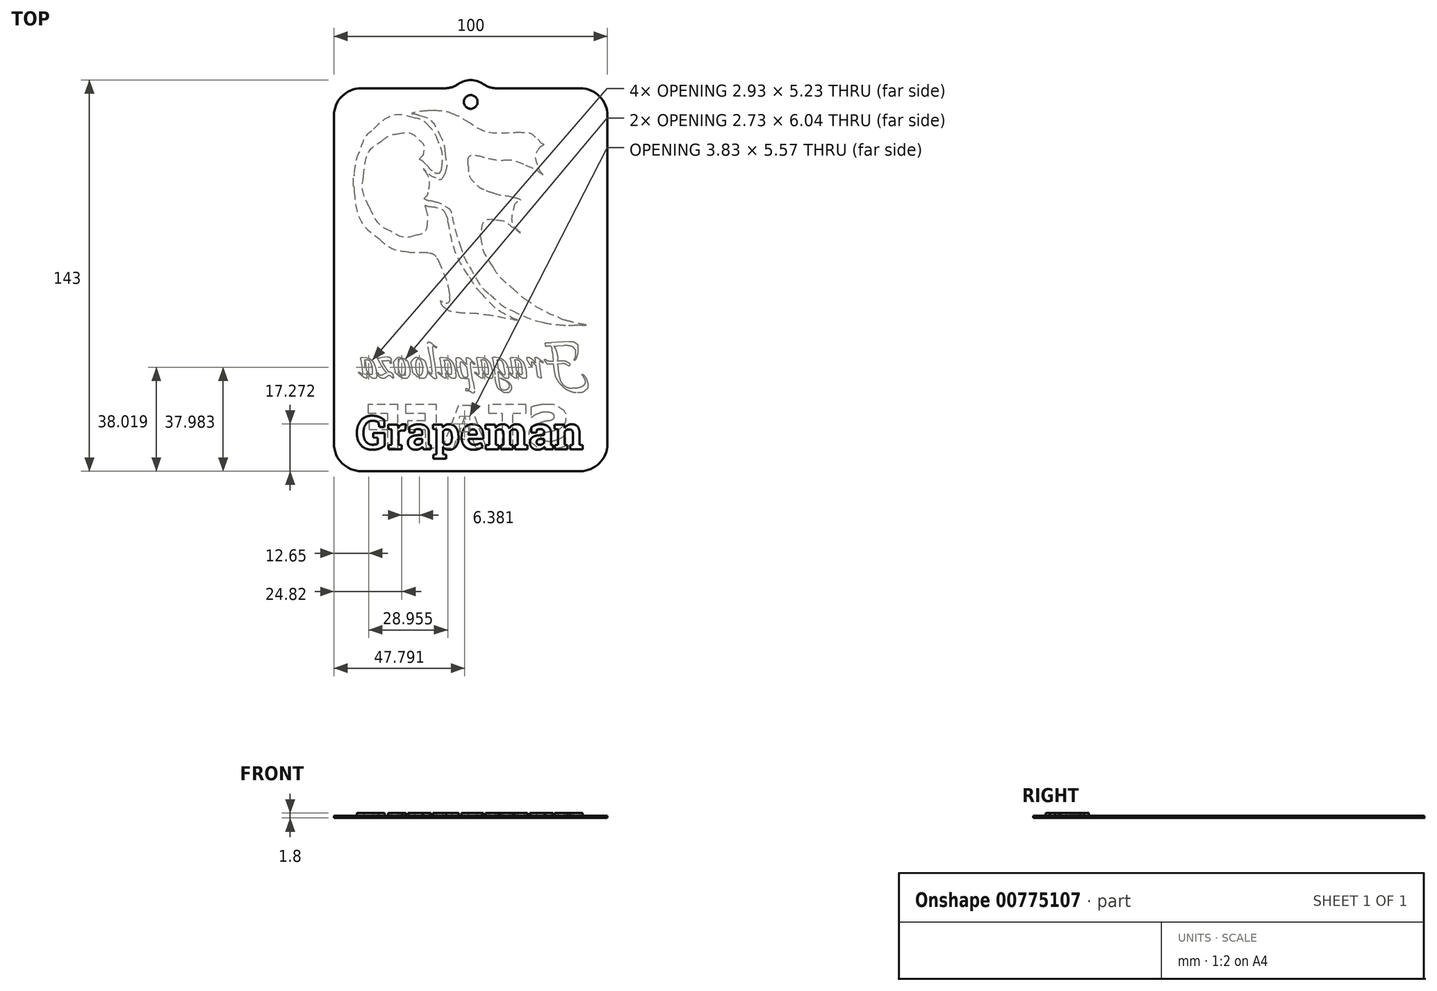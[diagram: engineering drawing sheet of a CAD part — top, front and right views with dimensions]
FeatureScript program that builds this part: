
annotation { "Feature Type Name" : "Feature", "Feature Type Description" : "" }
export const myFeature = defineFeature(function(context is Context, id is Id, definition is map)
    precondition{}
    {
        {
            var Q0;
            Q0=qCreatedBy(makeId("Top.planeOp"),FACE);
            var sketch = newSketch(context, id + "F0", { "sketchPlane" : qUnion([Q0])});
            skLineSegment(sketch, "E0.bottom", {"start": v(-40, 70) * mm, "end": v(-9.33, 70) * mm});
            skLineSegment(sketch, "E0.top", {"start": v(-40, -70) * mm, "end": v(40, -70) * mm});
            skLineSegment(sketch, "E0.left", {"start": v(-50, 60) * mm, "end": v(-50, -60) * mm});
            skLineSegment(sketch, "E0.right", {"start": v(50, 60) * mm, "end": v(50, -60) * mm});
            skPoint(sketch, "E0.middle", {"position": v(0, 0) * mm});
            skCircle(sketch, "E1", {"center": v(0, 65) * mm, "radius": 2.5 * mm});
            skPoint(sketch, "E2.visualSharp", {"position": v(-50, 70) * mm});
            skArc(sketch, "E2.filletArc", {"start": v(-40, 70) * mm, "mid": v(-47.07, 67.07) * mm, "end": v(-50, 60) * mm});
            skPoint(sketch, "E3.visualSharp", {"position": v(50, 70) * mm});
            skArc(sketch, "E3.filletArc", {"start": v(50, 60) * mm, "mid": v(47.07, 67.07) * mm, "end": v(40, 70) * mm});
            skPoint(sketch, "E4.visualSharp", {"position": v(50, -70) * mm});
            skArc(sketch, "E4.filletArc", {"start": v(40, -70) * mm, "mid": v(47.07, -67.07) * mm, "end": v(50, -60) * mm});
            skPoint(sketch, "E5.visualSharp", {"position": v(-50, -70) * mm});
            skArc(sketch, "E5.filletArc", {"start": v(-50, -60) * mm, "mid": v(-47.07, -67.07) * mm, "end": v(-40, -70) * mm});
            skArc(sketch, "E6", {"start": v(-4.66, 71.5) * mm, "mid": v(0, 73) * mm, "end": v(4.66, 71.5) * mm});
            skArc(sketch, "E7.filletArc", {"start": v(-9.33, 70) * mm, "mid": v(-6.88, 70.38) * mm, "end": v(-4.66, 71.5) * mm});
            skLineSegment(sketch, "E8", {"start": v(40, 70) * mm, "end": v(9.33, 70) * mm});
            skArc(sketch, "E9.filletArc", {"start": v(4.66, 71.5) * mm, "mid": v(6.88, 70.38) * mm, "end": v(9.33, 70) * mm});
            skSolve(sketch);
        }
        {
            var Q0;
            Q0=qCreatedBy(makeId("Top.planeOp"),FACE);
            var sketch = newSketch(context, id + "F1", { "sketchPlane" : qUnion([Q0])});
            skLineSegment(sketch, "E10", {"start": v(38.17, -16.7) * mm, "end": v(38.78, -16.7) * mm});
            skLineSegment(sketch, "E11", {"start": v(-13.07, 61.96) * mm, "end": v(-13.17, 61.96) * mm});
            skLineSegment(sketch, "E12", {"start": v(-14.17, 61.96) * mm, "end": v(-14.37, 61.96) * mm});
            skLineSegment(sketch, "E13", {"start": v(-42.85, 37.93) * mm, "end": v(-42.85, 36.81) * mm});
            skLineSegment(sketch, "E14", {"start": v(-42.85, 35.49) * mm, "end": v(-42.85, 34.98) * mm});
            skLineSegment(sketch, "E15", {"start": v(-42.85, 34.78) * mm, "end": v(-42.85, 34.16) * mm});
            skLineSegment(sketch, "E16", {"start": v(40.64, -16.7) * mm, "end": v(40.63, -16.62) * mm});
            skLineSegment(sketch, "E17", {"start": v(38.83, -16.7) * mm, "end": v(40.64, -16.7) * mm});
            skLineSegment(sketch, "E18", {"start": v(-42.85, 36.81) * mm, "end": v(-42.85, 35.49) * mm});
            skLineSegment(sketch, "E19", {"start": v(-13.21, 61.96) * mm, "end": v(-14.22, 61.96) * mm});
            skLineSegment(sketch, "E20", {"start": v(-42.85, 34.98) * mm, "end": v(-42.85, 34.77) * mm});
            skLineSegment(sketch, "E21", {"start": v(36.03, -31.52) * mm, "end": v(35.01, -30.98) * mm});
            skLineSegment(sketch, "E22", {"start": v(33.37, -30.7) * mm, "end": v(32.17, -30.75) * mm});
            skLineSegment(sketch, "E23", {"start": v(32.17, -30.75) * mm, "end": v(30.92, -30.82) * mm});
            skLineSegment(sketch, "E24", {"start": v(30.92, -30.82) * mm, "end": v(27.9, -30.82) * mm});
            skLineSegment(sketch, "E25", {"start": v(27.9, -30.82) * mm, "end": v(27.52, -30.26) * mm});
            skLineSegment(sketch, "E26", {"start": v(26.88, -29.35) * mm, "end": v(26.9, -29.28) * mm});
            skLineSegment(sketch, "E27", {"start": v(30.32, -29.76) * mm, "end": v(31.57, -29.76) * mm});
            skLineSegment(sketch, "E28", {"start": v(31.57, -29.76) * mm, "end": v(33.15, -29.76) * mm});
            skLineSegment(sketch, "E29", {"start": v(33.15, -29.76) * mm, "end": v(34.41, -29.76) * mm});
            skLineSegment(sketch, "E30", {"start": v(34.05, -24.06) * mm, "end": v(31.6, -24.16) * mm});
            skLineSegment(sketch, "E31", {"start": v(31.6, -24.16) * mm, "end": v(29.36, -24.3) * mm});
            skLineSegment(sketch, "E32", {"start": v(27.3, -24.39) * mm, "end": v(27.09, -23.13) * mm});
            skLineSegment(sketch, "E33", {"start": v(29.45, -22.97) * mm, "end": v(31.35, -22.93) * mm});
            skLineSegment(sketch, "E34", {"start": v(31.35, -22.93) * mm, "end": v(33.78, -22.78) * mm});
            skLineSegment(sketch, "E35", {"start": v(33.78, -22.78) * mm, "end": v(36.14, -22.66) * mm});
            skLineSegment(sketch, "E36", {"start": v(38.04, -29.5) * mm, "end": v(37.7, -29.32) * mm});
            skLineSegment(sketch, "E37", {"start": v(30.25, -30.2) * mm, "end": v(29.88, -26.54) * mm});
            skLineSegment(sketch, "E38", {"start": v(29.55, -24.56) * mm, "end": v(29.3, -24.3) * mm});
            skLineSegment(sketch, "E39", {"start": v(29.18, -23.96) * mm, "end": v(29.55, -24.04) * mm});
            skLineSegment(sketch, "E40", {"start": v(31.76, -29.06) * mm, "end": v(31.88, -31.82) * mm});
            skLineSegment(sketch, "E41", {"start": v(37.27, -39.71) * mm, "end": v(38.3, -39.63) * mm});
            skLineSegment(sketch, "E42", {"start": v(41.15, -35.4) * mm, "end": v(40.78, -34.92) * mm});
            skLineSegment(sketch, "E43", {"start": v(40.78, -34.92) * mm, "end": v(40.72, -34.76) * mm});
            skLineSegment(sketch, "E44", {"start": v(23.56, -29.53) * mm, "end": v(23.5, -28.89) * mm});
            skLineSegment(sketch, "E45", {"start": v(24.23, -28.54) * mm, "end": v(25.22, -29.23) * mm});
            skLineSegment(sketch, "E46", {"start": v(25.22, -29.23) * mm, "end": v(26.33, -30.01) * mm});
            skLineSegment(sketch, "E47", {"start": v(26.48, -30.3) * mm, "end": v(26.4, -30.34) * mm});
            skLineSegment(sketch, "E48", {"start": v(26.4, -30.34) * mm, "end": v(26.3, -30.32) * mm});
            skLineSegment(sketch, "E49", {"start": v(26.3, -30.32) * mm, "end": v(26.17, -30.3) * mm});
            skLineSegment(sketch, "E50", {"start": v(25.15, -30.3) * mm, "end": v(25.53, -33.54) * mm});
            skLineSegment(sketch, "E51", {"start": v(25.53, -33.54) * mm, "end": v(25.79, -35.64) * mm});
            skLineSegment(sketch, "E52", {"start": v(25.88, -36) * mm, "end": v(24.4, -35.44) * mm});
            skLineSegment(sketch, "E53", {"start": v(23.19, -29.85) * mm, "end": v(23.89, -30.75) * mm});
            skLineSegment(sketch, "E54", {"start": v(23.65, -31.18) * mm, "end": v(23.19, -30.77) * mm});
            skLineSegment(sketch, "E55", {"start": v(15.9, -29.4) * mm, "end": v(15.4, -29.4) * mm});
            skLineSegment(sketch, "E56", {"start": v(15.4, -29.4) * mm, "end": v(15.02, -29.33) * mm});
            skLineSegment(sketch, "E57", {"start": v(15.24, -28.42) * mm, "end": v(16.71, -28.55) * mm});
            skLineSegment(sketch, "E58", {"start": v(17.3, -34.56) * mm, "end": v(16.63, -33.84) * mm});
            skLineSegment(sketch, "E59", {"start": v(16.01, -32.3) * mm, "end": v(16.46, -32.84) * mm});
            skLineSegment(sketch, "E60", {"start": v(16.96, -29.4) * mm, "end": v(16.5, -29.4) * mm});
            skLineSegment(sketch, "E61", {"start": v(16.5, -29.4) * mm, "end": v(15.9, -29.4) * mm});
            skLineSegment(sketch, "E62", {"start": v(16.38, -31.1) * mm, "end": v(16.6, -32.79) * mm});
            skLineSegment(sketch, "E63", {"start": v(16.6, -32.79) * mm, "end": v(16.8, -34.4) * mm});
            skLineSegment(sketch, "E64", {"start": v(16.8, -34.4) * mm, "end": v(16.85, -35.3) * mm});
            skLineSegment(sketch, "E65", {"start": v(14.85, -34.45) * mm, "end": v(15.26, -34.75) * mm});
            skLineSegment(sketch, "E66", {"start": v(15.33, -34.51) * mm, "end": v(15.26, -33.72) * mm});
            skLineSegment(sketch, "E67", {"start": v(15.26, -33.72) * mm, "end": v(14.93, -31.64) * mm});
            skLineSegment(sketch, "E68", {"start": v(14.93, -31.64) * mm, "end": v(14.54, -29.14) * mm});
            skLineSegment(sketch, "E69", {"start": v(9.13, -29.4) * mm, "end": v(8.63, -29.4) * mm});
            skLineSegment(sketch, "E70", {"start": v(8.63, -29.4) * mm, "end": v(8.27, -29.31) * mm});
            skLineSegment(sketch, "E71", {"start": v(8.04, -29.08) * mm, "end": v(7.89, -28.74) * mm});
            skLineSegment(sketch, "E72", {"start": v(8.47, -28.35) * mm, "end": v(8.95, -28.35) * mm});
            skLineSegment(sketch, "E73", {"start": v(8.95, -28.35) * mm, "end": v(9.46, -28.52) * mm});
            skLineSegment(sketch, "E74", {"start": v(9.46, -28.52) * mm, "end": v(10.14, -28.6) * mm});
            skLineSegment(sketch, "E75", {"start": v(11.28, -34.74) * mm, "end": v(10.47, -33.88) * mm});
            skLineSegment(sketch, "E76", {"start": v(9.69, -32.05) * mm, "end": v(10.37, -32.95) * mm});
            skLineSegment(sketch, "E77", {"start": v(10.37, -32.95) * mm, "end": v(11.14, -33.94) * mm});
            skLineSegment(sketch, "E78", {"start": v(12.6, -34.13) * mm, "end": v(12.52, -33.32) * mm});
            skLineSegment(sketch, "E79", {"start": v(12.52, -33.32) * mm, "end": v(12.29, -32.26) * mm});
            skLineSegment(sketch, "E80", {"start": v(12.29, -32.26) * mm, "end": v(12.13, -31.6) * mm});
            skLineSegment(sketch, "E81", {"start": v(10.33, -29.4) * mm, "end": v(9.77, -29.4) * mm});
            skLineSegment(sketch, "E82", {"start": v(9.77, -29.4) * mm, "end": v(9.13, -29.4) * mm});
            skLineSegment(sketch, "E83", {"start": v(9.46, -28.84) * mm, "end": v(9.77, -30.97) * mm});
            skLineSegment(sketch, "E84", {"start": v(9.77, -30.97) * mm, "end": v(10.1, -34.04) * mm});
            skLineSegment(sketch, "E85", {"start": v(10.1, -34.04) * mm, "end": v(10.34, -36.29) * mm});
            skLineSegment(sketch, "E86", {"start": v(10.34, -36.29) * mm, "end": v(10.47, -37.68) * mm});
            skLineSegment(sketch, "E87", {"start": v(12.25, -36.7) * mm, "end": v(11.22, -36.28) * mm});
            skLineSegment(sketch, "E88", {"start": v(10.66, -36) * mm, "end": v(10.7, -35.94) * mm});
            skLineSegment(sketch, "E89", {"start": v(8.88, -35.3) * mm, "end": v(8.5, -31.75) * mm});
            skLineSegment(sketch, "E90", {"start": v(3.54, -29.4) * mm, "end": v(3.04, -29.4) * mm});
            skLineSegment(sketch, "E91", {"start": v(3.04, -29.4) * mm, "end": v(2.67, -29.33) * mm});
            skLineSegment(sketch, "E92", {"start": v(2.88, -28.42) * mm, "end": v(4.36, -28.55) * mm});
            skLineSegment(sketch, "E93", {"start": v(4.94, -34.56) * mm, "end": v(4.28, -33.84) * mm});
            skLineSegment(sketch, "E94", {"start": v(3.66, -32.3) * mm, "end": v(4.1, -32.84) * mm});
            skLineSegment(sketch, "E95", {"start": v(4.6, -29.4) * mm, "end": v(4.14, -29.4) * mm});
            skLineSegment(sketch, "E96", {"start": v(4.14, -29.4) * mm, "end": v(3.54, -29.4) * mm});
            skLineSegment(sketch, "E97", {"start": v(4.02, -31.1) * mm, "end": v(4.25, -32.79) * mm});
            skLineSegment(sketch, "E98", {"start": v(4.25, -32.79) * mm, "end": v(4.44, -34.4) * mm});
            skLineSegment(sketch, "E99", {"start": v(4.44, -34.4) * mm, "end": v(4.5, -35.3) * mm});
            skLineSegment(sketch, "E100", {"start": v(2.5, -34.45) * mm, "end": v(2.9, -34.75) * mm});
            skLineSegment(sketch, "E101", {"start": v(2.98, -34.51) * mm, "end": v(2.9, -33.72) * mm});
            skLineSegment(sketch, "E102", {"start": v(2.9, -33.72) * mm, "end": v(2.58, -31.64) * mm});
            skLineSegment(sketch, "E103", {"start": v(2.58, -31.64) * mm, "end": v(2.19, -29.14) * mm});
            skLineSegment(sketch, "E104", {"start": v(-0.07, -30.77) * mm, "end": v(0.03, -32.01) * mm});
            skLineSegment(sketch, "E105", {"start": v(0.03, -32.01) * mm, "end": v(0.35, -34.14) * mm});
            skLineSegment(sketch, "E106", {"start": v(0.35, -34.14) * mm, "end": v(0.85, -37.11) * mm});
            skLineSegment(sketch, "E107", {"start": v(0.96, -41.4) * mm, "end": v(0.32, -41.16) * mm});
            skLineSegment(sketch, "E108", {"start": v(-0.43, -39.67) * mm, "end": v(-0.47, -38.83) * mm});
            skLineSegment(sketch, "E109", {"start": v(-0.47, -38.83) * mm, "end": v(-0.77, -36.7) * mm});
            skLineSegment(sketch, "E110", {"start": v(-0.77, -36.7) * mm, "end": v(-1.14, -33.74) * mm});
            skLineSegment(sketch, "E111", {"start": v(-1.14, -33.74) * mm, "end": v(-1.34, -32.16) * mm});
            skLineSegment(sketch, "E112", {"start": v(-1.34, -32.16) * mm, "end": v(-1.56, -30.34) * mm});
            skLineSegment(sketch, "E113", {"start": v(-1.56, -30.34) * mm, "end": v(-1.62, -29.37) * mm});
            skLineSegment(sketch, "E114", {"start": v(-0.41, -35.45) * mm, "end": v(-0.36, -35.65) * mm});
            skLineSegment(sketch, "E115", {"start": v(-0.18, -36.1) * mm, "end": v(-0.24, -36.16) * mm});
            skLineSegment(sketch, "E116", {"start": v(-0.24, -36.16) * mm, "end": v(-0.31, -36.19) * mm});
            skLineSegment(sketch, "E117", {"start": v(-0.31, -36.19) * mm, "end": v(-0.7, -36.11) * mm});
            skLineSegment(sketch, "E118", {"start": v(-0.7, -36.11) * mm, "end": v(-1.4, -36.11) * mm});
            skLineSegment(sketch, "E119", {"start": v(-1.4, -36.11) * mm, "end": v(-2.27, -36.11) * mm});
            skLineSegment(sketch, "E120", {"start": v(-2.53, -30.03) * mm, "end": v(-1.85, -30.67) * mm});
            skLineSegment(sketch, "E121", {"start": v(-9.94, -29.4) * mm, "end": v(-10.44, -29.4) * mm});
            skLineSegment(sketch, "E122", {"start": v(-10.44, -29.4) * mm, "end": v(-10.8, -29.33) * mm});
            skLineSegment(sketch, "E123", {"start": v(-10.6, -28.42) * mm, "end": v(-9.12, -28.55) * mm});
            skLineSegment(sketch, "E124", {"start": v(-8.54, -34.56) * mm, "end": v(-9.2, -33.84) * mm});
            skLineSegment(sketch, "E125", {"start": v(-9.82, -32.3) * mm, "end": v(-9.37, -32.84) * mm});
            skLineSegment(sketch, "E126", {"start": v(-8.87, -29.4) * mm, "end": v(-9.34, -29.4) * mm});
            skLineSegment(sketch, "E127", {"start": v(-9.34, -29.4) * mm, "end": v(-9.94, -29.4) * mm});
            skLineSegment(sketch, "E128", {"start": v(-9.46, -31.1) * mm, "end": v(-9.23, -32.79) * mm});
            skLineSegment(sketch, "E129", {"start": v(-9.23, -32.79) * mm, "end": v(-9.04, -34.4) * mm});
            skLineSegment(sketch, "E130", {"start": v(-9.04, -34.4) * mm, "end": v(-8.99, -35.3) * mm});
            skLineSegment(sketch, "E131", {"start": v(-10.98, -34.45) * mm, "end": v(-10.58, -34.75) * mm});
            skLineSegment(sketch, "E132", {"start": v(-10.5, -34.51) * mm, "end": v(-10.58, -33.72) * mm});
            skLineSegment(sketch, "E133", {"start": v(-10.58, -33.72) * mm, "end": v(-10.9, -31.64) * mm});
            skLineSegment(sketch, "E134", {"start": v(-10.9, -31.64) * mm, "end": v(-11.29, -29.14) * mm});
            skLineSegment(sketch, "E135", {"start": v(-14.16, -33.74) * mm, "end": v(-14.26, -32.52) * mm});
            skLineSegment(sketch, "E136", {"start": v(-14.26, -32.52) * mm, "end": v(-14.56, -30.46) * mm});
            skLineSegment(sketch, "E137", {"start": v(-14.56, -30.46) * mm, "end": v(-15.08, -27.43) * mm});
            skLineSegment(sketch, "E138", {"start": v(-15, -22.92) * mm, "end": v(-14.03, -23.56) * mm});
            skLineSegment(sketch, "E139", {"start": v(-12.63, -24.87) * mm, "end": v(-12.86, -24.8) * mm});
            skLineSegment(sketch, "E140", {"start": v(-13.91, -24.76) * mm, "end": v(-13.85, -25.5) * mm});
            skLineSegment(sketch, "E141", {"start": v(-13.85, -25.5) * mm, "end": v(-13.65, -26.9) * mm});
            skLineSegment(sketch, "E142", {"start": v(-13.65, -26.9) * mm, "end": v(-13.36, -28.73) * mm});
            skLineSegment(sketch, "E143", {"start": v(-13.36, -28.73) * mm, "end": v(-13.08, -30.79) * mm});
            skLineSegment(sketch, "E144", {"start": v(-13.08, -30.79) * mm, "end": v(-12.8, -32.84) * mm});
            skLineSegment(sketch, "E145", {"start": v(-12.8, -32.84) * mm, "end": v(-12.61, -34.45) * mm});
            skLineSegment(sketch, "E146", {"start": v(-12.61, -34.45) * mm, "end": v(-12.55, -35.39) * mm});
            skLineSegment(sketch, "E147", {"start": v(-19.13, -35.54) * mm, "end": v(-20.12, -34.9) * mm});
            skLineSegment(sketch, "E148", {"start": v(-21.26, -33.55) * mm, "end": v(-21.5, -32.5) * mm});
            skLineSegment(sketch, "E149", {"start": v(-21.5, -32.5) * mm, "end": v(-21.73, -31.52) * mm});
            skLineSegment(sketch, "E150", {"start": v(-21.73, -31.52) * mm, "end": v(-21.79, -30.84) * mm});
            skLineSegment(sketch, "E151", {"start": v(-19.8, -28.37) * mm, "end": v(-19.36, -28.42) * mm});
            skLineSegment(sketch, "E152", {"start": v(-19.36, -28.42) * mm, "end": v(-18.37, -28.75) * mm});
            skLineSegment(sketch, "E153", {"start": v(-17.54, -31.66) * mm, "end": v(-18, -30.05) * mm});
            skLineSegment(sketch, "E154", {"start": v(-25.5, -35.54) * mm, "end": v(-26.5, -34.9) * mm});
            skLineSegment(sketch, "E155", {"start": v(-27.64, -33.55) * mm, "end": v(-27.88, -32.5) * mm});
            skLineSegment(sketch, "E156", {"start": v(-27.88, -32.5) * mm, "end": v(-28.1, -31.52) * mm});
            skLineSegment(sketch, "E157", {"start": v(-28.1, -31.52) * mm, "end": v(-28.17, -30.84) * mm});
            skLineSegment(sketch, "E158", {"start": v(-26.19, -28.37) * mm, "end": v(-25.74, -28.42) * mm});
            skLineSegment(sketch, "E159", {"start": v(-25.74, -28.42) * mm, "end": v(-24.75, -28.75) * mm});
            skLineSegment(sketch, "E160", {"start": v(-23.92, -31.66) * mm, "end": v(-24.38, -30.05) * mm});
            skLineSegment(sketch, "E161", {"start": v(-30.82, -29.63) * mm, "end": v(-31.6, -29.66) * mm});
            skLineSegment(sketch, "E162", {"start": v(-31.6, -29.66) * mm, "end": v(-32.28, -29.63) * mm});
            skLineSegment(sketch, "E163", {"start": v(-32.28, -29.63) * mm, "end": v(-32.6, -29.59) * mm});
            skLineSegment(sketch, "E164", {"start": v(-28.05, -35.7) * mm, "end": v(-28.34, -36) * mm});
            skLineSegment(sketch, "E165", {"start": v(-32.16, -32.19) * mm, "end": v(-32.67, -31.4) * mm});
            skLineSegment(sketch, "E166", {"start": v(-32.67, -31.4) * mm, "end": v(-33.23, -30.44) * mm});
            skLineSegment(sketch, "E167", {"start": v(-33.23, -30.44) * mm, "end": v(-33.8, -29.45) * mm});
            skLineSegment(sketch, "E168", {"start": v(-33.8, -29.45) * mm, "end": v(-34.28, -28.64) * mm});
            skLineSegment(sketch, "E169", {"start": v(-34.18, -28.33) * mm, "end": v(-34.02, -28.38) * mm});
            skLineSegment(sketch, "E170", {"start": v(-33.17, -28.56) * mm, "end": v(-32.43, -28.52) * mm});
            skLineSegment(sketch, "E171", {"start": v(-32.43, -28.52) * mm, "end": v(-31.52, -28.4) * mm});
            skLineSegment(sketch, "E172", {"start": v(-31.52, -28.4) * mm, "end": v(-30.4, -28.23) * mm});
            skLineSegment(sketch, "E173", {"start": v(-29.1, -29.33) * mm, "end": v(-29.02, -30) * mm});
            skLineSegment(sketch, "E174", {"start": v(-28.09, -35.68) * mm, "end": v(-28.22, -35.85) * mm});
            skLineSegment(sketch, "E175", {"start": v(-28.4, -35.95) * mm, "end": v(-29.27, -35.27) * mm});
            skLineSegment(sketch, "E176", {"start": v(-32.12, -34.67) * mm, "end": v(-31.13, -34.22) * mm});
            skLineSegment(sketch, "E177", {"start": v(-31.13, -34.22) * mm, "end": v(-30.22, -33.8) * mm});
            skLineSegment(sketch, "E178", {"start": v(-28.36, -35.08) * mm, "end": v(-28.32, -35.29) * mm});
            skLineSegment(sketch, "E179", {"start": v(-28.32, -35.29) * mm, "end": v(-28.26, -35.48) * mm});
            skLineSegment(sketch, "E180", {"start": v(-28.26, -35.48) * mm, "end": v(-28.09, -35.68) * mm});
            skLineSegment(sketch, "E181", {"start": v(-38.9, -29.4) * mm, "end": v(-39.4, -29.4) * mm});
            skLineSegment(sketch, "E182", {"start": v(-39.4, -29.4) * mm, "end": v(-39.76, -29.33) * mm});
            skLineSegment(sketch, "E183", {"start": v(-39.55, -28.42) * mm, "end": v(-38.08, -28.55) * mm});
            skLineSegment(sketch, "E184", {"start": v(-37.5, -34.56) * mm, "end": v(-38.15, -33.84) * mm});
            skLineSegment(sketch, "E185", {"start": v(-38.77, -32.3) * mm, "end": v(-38.33, -32.84) * mm});
            skLineSegment(sketch, "E186", {"start": v(-37.82, -29.4) * mm, "end": v(-38.3, -29.4) * mm});
            skLineSegment(sketch, "E187", {"start": v(-38.3, -29.4) * mm, "end": v(-38.9, -29.4) * mm});
            skLineSegment(sketch, "E188", {"start": v(-38.41, -31.1) * mm, "end": v(-38.19, -32.79) * mm});
            skLineSegment(sketch, "E189", {"start": v(-38.19, -32.79) * mm, "end": v(-38, -34.4) * mm});
            skLineSegment(sketch, "E190", {"start": v(-38, -34.4) * mm, "end": v(-37.94, -35.3) * mm});
            skLineSegment(sketch, "E191", {"start": v(-39.94, -34.45) * mm, "end": v(-39.53, -34.75) * mm});
            skLineSegment(sketch, "E192", {"start": v(-39.45, -34.51) * mm, "end": v(-39.53, -33.72) * mm});
            skLineSegment(sketch, "E193", {"start": v(-39.53, -33.72) * mm, "end": v(-39.86, -31.64) * mm});
            skLineSegment(sketch, "E194", {"start": v(-39.86, -31.64) * mm, "end": v(-40.24, -29.14) * mm});
            skLineSegment(sketch, "E195", {"start": v(22.49, -50.22) * mm, "end": v(22.06, -50.22) * mm});
            skLineSegment(sketch, "E196", {"start": v(22.06, -50.22) * mm, "end": v(22.06, -46.56) * mm});
            skLineSegment(sketch, "E197", {"start": v(34.32, -56.92) * mm, "end": v(34.76, -56.92) * mm});
            skLineSegment(sketch, "E198", {"start": v(34.76, -56.92) * mm, "end": v(34.76, -60.73) * mm});
            skLineSegment(sketch, "E199", {"start": v(6.54, -45.64) * mm, "end": v(20.3, -45.64) * mm});
            skLineSegment(sketch, "E200", {"start": v(20.3, -45.64) * mm, "end": v(20.3, -48.81) * mm});
            skLineSegment(sketch, "E201", {"start": v(20.3, -48.81) * mm, "end": v(15.36, -48.81) * mm});
            skLineSegment(sketch, "E202", {"start": v(15.36, -48.81) * mm, "end": v(15.36, -61.51) * mm});
            skLineSegment(sketch, "E203", {"start": v(15.36, -61.51) * mm, "end": v(11.47, -61.51) * mm});
            skLineSegment(sketch, "E204", {"start": v(11.47, -61.51) * mm, "end": v(11.47, -48.81) * mm});
            skLineSegment(sketch, "E205", {"start": v(11.47, -48.81) * mm, "end": v(6.54, -48.81) * mm});
            skLineSegment(sketch, "E206", {"start": v(6.54, -48.81) * mm, "end": v(6.54, -45.64) * mm});
            skLineSegment(sketch, "E207", {"start": v(-4.56, -45.99) * mm, "end": v(0.04, -45.99) * mm});
            skLineSegment(sketch, "E208", {"start": v(0.04, -45.99) * mm, "end": v(5.78, -61.51) * mm});
            skLineSegment(sketch, "E209", {"start": v(5.78, -61.51) * mm, "end": v(1.8, -61.51) * mm});
            skLineSegment(sketch, "E210", {"start": v(1.8, -61.51) * mm, "end": v(0.7, -58.34) * mm});
            skLineSegment(sketch, "E211", {"start": v(0.7, -58.34) * mm, "end": v(-5.12, -58.34) * mm});
            skLineSegment(sketch, "E212", {"start": v(-5.12, -58.34) * mm, "end": v(-6.2, -61.51) * mm});
            skLineSegment(sketch, "E213", {"start": v(-6.2, -61.51) * mm, "end": v(-10.3, -61.51) * mm});
            skLineSegment(sketch, "E214", {"start": v(-10.3, -61.51) * mm, "end": v(-4.56, -45.99) * mm});
            skLineSegment(sketch, "E215", {"start": v(-0.3, -55.51) * mm, "end": v(-2.2, -49.94) * mm});
            skLineSegment(sketch, "E216", {"start": v(-2.2, -49.94) * mm, "end": v(-4.12, -55.51) * mm});
            skLineSegment(sketch, "E217", {"start": v(-4.12, -55.51) * mm, "end": v(-0.3, -55.51) * mm});
            skLineSegment(sketch, "E218", {"start": v(-23.8, -45.64) * mm, "end": v(-12.51, -45.64) * mm});
            skLineSegment(sketch, "E219", {"start": v(-12.51, -45.64) * mm, "end": v(-12.51, -61.51) * mm});
            skLineSegment(sketch, "E220", {"start": v(-12.51, -61.51) * mm, "end": v(-16.4, -61.51) * mm});
            skLineSegment(sketch, "E221", {"start": v(-16.4, -61.51) * mm, "end": v(-16.75, -54.8) * mm});
            skLineSegment(sketch, "E222", {"start": v(-16.75, -54.8) * mm, "end": v(-23.1, -54.8) * mm});
            skLineSegment(sketch, "E223", {"start": v(-23.1, -54.8) * mm, "end": v(-23.1, -51.63) * mm});
            skLineSegment(sketch, "E224", {"start": v(-23.1, -51.63) * mm, "end": v(-16.75, -51.63) * mm});
            skLineSegment(sketch, "E225", {"start": v(-16.75, -51.63) * mm, "end": v(-16.75, -48.81) * mm});
            skLineSegment(sketch, "E226", {"start": v(-16.75, -48.81) * mm, "end": v(-23.8, -48.81) * mm});
            skLineSegment(sketch, "E227", {"start": v(-23.8, -48.81) * mm, "end": v(-23.8, -45.64) * mm});
            skLineSegment(sketch, "E228", {"start": v(-37.56, -45.64) * mm, "end": v(-26.63, -45.64) * mm});
            skLineSegment(sketch, "E229", {"start": v(-26.63, -45.64) * mm, "end": v(-26.63, -61.51) * mm});
            skLineSegment(sketch, "E230", {"start": v(-26.63, -61.51) * mm, "end": v(-30.5, -61.51) * mm});
            skLineSegment(sketch, "E231", {"start": v(-30.5, -61.51) * mm, "end": v(-30.5, -54.8) * mm});
            skLineSegment(sketch, "E232", {"start": v(-30.5, -54.8) * mm, "end": v(-37.2, -54.8) * mm});
            skLineSegment(sketch, "E233", {"start": v(-37.2, -54.8) * mm, "end": v(-37.2, -51.63) * mm});
            skLineSegment(sketch, "E234", {"start": v(-37.2, -51.63) * mm, "end": v(-30.5, -51.63) * mm});
            skLineSegment(sketch, "E235", {"start": v(-30.5, -51.63) * mm, "end": v(-30.5, -48.81) * mm});
            skLineSegment(sketch, "E236", {"start": v(-30.5, -48.81) * mm, "end": v(-37.56, -48.81) * mm});
            skLineSegment(sketch, "E237", {"start": v(-37.56, -48.81) * mm, "end": v(-37.56, -45.64) * mm});
            skFitSpline(sketch, "E238", {"points": [v(-14.37, 61.96) * mm, v(-14.8, 61.78) * mm, v(-15.26, 61.8) * mm, v(-15.71, 61.76) * mm]});
            skFitSpline(sketch, "E239", {"points": [v(-15.71, 61.76) * mm, v(-17.53, 61.62) * mm, v(-19.32, 61.38) * mm, v(-21.1, 60.93) * mm]});
            skFitSpline(sketch, "E240", {"points": [v(-21.1, 60.93) * mm, v(-21.24, 60.9) * mm, v(-21.43, 60.9) * mm, v(-21.54, 60.66) * mm]});
            skFitSpline(sketch, "E241", {"points": [v(-21.54, 60.66) * mm, v(-20.54, 60.63) * mm, v(-19.62, 60.35) * mm, v(-18.7, 60.03) * mm]});
            skFitSpline(sketch, "E242", {"points": [v(-18.7, 60.03) * mm, v(-15.38, 58.87) * mm, v(-13.15, 56.52) * mm, v(-11.58, 53.44) * mm]});
            skFitSpline(sketch, "E243", {"points": [v(-11.58, 53.44) * mm, v(-10.47, 51.29) * mm, v(-9.71, 49) * mm, v(-9.41, 46.6) * mm]});
            skFitSpline(sketch, "E244", {"points": [v(-9.41, 46.6) * mm, v(-9.11, 44.15) * mm, v(-8.77, 41.68) * mm, v(-9.35, 39.2) * mm]});
            skFitSpline(sketch, "E245", {"points": [v(-9.35, 39.2) * mm, v(-9.4, 38.94) * mm, v(-9.5, 38.7) * mm, v(-9.63, 38.47) * mm]});
            skFitSpline(sketch, "E246", {"points": [v(-9.63, 38.47) * mm, v(-10.22, 37.39) * mm, v(-11.1, 36.57) * mm, v(-12.72, 37.2) * mm]});
            skFitSpline(sketch, "E247", {"points": [v(-12.72, 37.2) * mm, v(-14.12, 37.75) * mm, v(-15.28, 38.64) * mm, v(-16.36, 39.65) * mm]});
            skFitSpline(sketch, "E248", {"points": [v(-16.36, 39.65) * mm, v(-16.66, 39.92) * mm, v(-16.91, 40.23) * mm, v(-17.25, 40.59) * mm]});
            skFitSpline(sketch, "E249", {"points": [v(-17.25, 40.59) * mm, v(-17.26, 40.3) * mm, v(-17.11, 40.19) * mm, v(-17.03, 40.05) * mm]});
            skFitSpline(sketch, "E250", {"points": [v(-17.03, 40.05) * mm, v(-15.47, 37.53) * mm, v(-15.17, 34.78) * mm, v(-15.68, 31.91) * mm]});
            skFitSpline(sketch, "E251", {"points": [v(-15.68, 31.91) * mm, v(-15.8, 31.24) * mm, v(-16.1, 30.64) * mm, v(-16.6, 30.16) * mm]});
            skFitSpline(sketch, "E252", {"points": [v(-16.6, 30.16) * mm, v(-17.12, 29.67) * mm, v(-17.1, 29.65) * mm, v(-16.44, 29.37) * mm]});
            skFitSpline(sketch, "E253", {"points": [v(-16.44, 29.37) * mm, v(-15.51, 28.97) * mm, v(-14.51, 28.87) * mm, v(-13.54, 28.62) * mm]});
            skFitSpline(sketch, "E254", {"points": [v(-13.54, 28.62) * mm, v(-11.87, 28.2) * mm, v(-10.3, 27.56) * mm, v(-8.86, 26.56) * mm]});
            skFitSpline(sketch, "E255", {"points": [v(-8.86, 26.56) * mm, v(-7.66, 25.72) * mm, v(-7.05, 24.5) * mm, v(-6.77, 23.12) * mm]});
            skFitSpline(sketch, "E256", {"points": [v(-6.77, 23.12) * mm, v(-6.07, 19.68) * mm, v(-5.15, 16.3) * mm, v(-4.03, 13) * mm]});
            skFitSpline(sketch, "E257", {"points": [v(-4.03, 13) * mm, v(-3.06, 10.12) * mm, v(-1.94, 7.3) * mm, v(-0.43, 4.69) * mm]});
            skFitSpline(sketch, "E258", {"points": [v(-0.43, 4.69) * mm, v(1.68, 1.04) * mm, v(3.89, -2.54) * mm, v(7.02, -5.42) * mm]});
            skFitSpline(sketch, "E259", {"points": [v(7.02, -5.42) * mm, v(9.48, -7.68) * mm, v(12.02, -9.8) * mm, v(15.04, -11.25) * mm]});
            skFitSpline(sketch, "E260", {"points": [v(15.04, -11.25) * mm, v(18.76, -13.03) * mm, v(22.58, -14.59) * mm, v(26.59, -15.61) * mm]});
            skFitSpline(sketch, "E261", {"points": [v(26.59, -15.61) * mm, v(28.25, -16.04) * mm, v(29.96, -16.23) * mm, v(31.67, -16.4) * mm]});
            skFitSpline(sketch, "E262", {"points": [v(31.67, -16.4) * mm, v(33.03, -16.54) * mm, v(34.4, -16.62) * mm, v(35.77, -16.62) * mm]});
            skFitSpline(sketch, "E263", {"points": [v(35.77, -16.62) * mm, v(36.22, -16.7) * mm, v(36.67, -16.64) * mm, v(37.13, -16.66) * mm]});
            skFitSpline(sketch, "E264", {"points": [v(37.13, -16.66) * mm, v(37.48, -16.68) * mm, v(37.83, -16.6) * mm, v(38.17, -16.7) * mm]});
            skFitSpline(sketch, "E265", {"points": [v(38.78, -16.7) * mm, v(39.38, -16.6) * mm, v(39.99, -16.69) * mm, v(40.59, -16.66) * mm]});
            skFitSpline(sketch, "E266", {"points": [v(40.59, -16.66) * mm, v(41.03, -16.65) * mm, v(41.48, -16.66) * mm, v(41.92, -16.65) * mm]});
            skFitSpline(sketch, "E267", {"points": [v(41.92, -16.65) * mm, v(42.02, -16.65) * mm, v(42.17, -16.71) * mm, v(42.18, -16.52) * mm]});
            skFitSpline(sketch, "E268", {"points": [v(42.18, -16.52) * mm, v(40.35, -16.18) * mm, v(38.52, -15.83) * mm, v(36.71, -15.35) * mm]});
            skFitSpline(sketch, "E269", {"points": [v(36.71, -15.35) * mm, v(36, -15.16) * mm, v(35.25, -15.03) * mm, v(34.53, -14.82) * mm]});
            skFitSpline(sketch, "E270", {"points": [v(34.53, -14.82) * mm, v(33.1, -14.38) * mm, v(31.81, -13.6) * mm, v(30.4, -13.1) * mm]});
            skFitSpline(sketch, "E271", {"points": [v(30.4, -13.1) * mm, v(28.9, -12.57) * mm, v(27.54, -11.75) * mm, v(26.13, -11.04) * mm]});
            skFitSpline(sketch, "E272", {"points": [v(26.13, -11.04) * mm, v(24.28, -10.1) * mm, v(22.61, -8.9) * mm, v(20.9, -7.78) * mm]});
            skFitSpline(sketch, "E273", {"points": [v(20.9, -7.78) * mm, v(19.32, -6.73) * mm, v(17.87, -5.46) * mm, v(16.43, -4.2) * mm]});
            skFitSpline(sketch, "E274", {"points": [v(16.43, -4.2) * mm, v(13.43, -1.57) * mm, v(10.5, 1.14) * mm, v(8.29, 4.51) * mm]});
            skFitSpline(sketch, "E275", {"points": [v(8.29, 4.51) * mm, v(6.39, 7.4) * mm, v(4.75, 10.42) * mm, v(4.04, 13.87) * mm]});
            skFitSpline(sketch, "E276", {"points": [v(4.04, 13.87) * mm, v(3.74, 15.29) * mm, v(3.6, 16.77) * mm, v(3.96, 18.15) * mm]});
            skFitSpline(sketch, "E277", {"points": [v(3.96, 18.15) * mm, v(4.68, 20.94) * mm, v(6.59, 22.1) * mm, v(9.37, 21.76) * mm]});
            skFitSpline(sketch, "E278", {"points": [v(9.37, 21.76) * mm, v(12.14, 21.42) * mm, v(14.36, 19.9) * mm, v(16.53, 18.28) * mm]});
            skFitSpline(sketch, "E279", {"points": [v(16.53, 18.28) * mm, v(17.05, 17.9) * mm, v(17.55, 17.5) * mm, v(18.06, 17.1) * mm]});
            skFitSpline(sketch, "E280", {"points": [v(18.06, 17.1) * mm, v(18.14, 17.24) * mm, v(18.06, 17.27) * mm, v(18.02, 17.3) * mm]});
            skFitSpline(sketch, "E281", {"points": [v(18.02, 17.3) * mm, v(15.67, 19.8) * mm, v(15.1, 22.76) * mm, v(15.81, 26.03) * mm]});
            skFitSpline(sketch, "E282", {"points": [v(15.81, 26.03) * mm, v(16.12, 27.45) * mm, v(16.96, 28.48) * mm, v(18.36, 29.08) * mm]});
            skFitSpline(sketch, "E283", {"points": [v(18.36, 29.08) * mm, v(17.45, 29.57) * mm, v(16.52, 29.83) * mm, v(15.58, 30.04) * mm]});
            skFitSpline(sketch, "E284", {"points": [v(15.58, 30.04) * mm, v(13.22, 30.57) * mm, v(10.83, 30.9) * mm, v(8.5, 31.57) * mm]});
            skFitSpline(sketch, "E285", {"points": [v(8.5, 31.57) * mm, v(7.27, 31.92) * mm, v(6.07, 32.36) * mm, v(4.9, 32.88) * mm]});
            skFitSpline(sketch, "E286", {"points": [v(4.9, 32.88) * mm, v(3.5, 33.5) * mm, v(2.36, 34.42) * mm, v(1.34, 35.53) * mm]});
            skFitSpline(sketch, "E287", {"points": [v(1.34, 35.53) * mm, v(0.04, 36.96) * mm, v(-0.59, 38.66) * mm, v(-0.74, 40.57) * mm]});
            skFitSpline(sketch, "E288", {"points": [v(-0.74, 40.57) * mm, v(-0.8, 41.38) * mm, v(-1, 42.17) * mm, v(-0.94, 43) * mm]});
            skFitSpline(sketch, "E289", {"points": [v(-0.94, 43) * mm, v(-0.85, 44.55) * mm, v(0.53, 45.67) * mm, v(2.04, 45.42) * mm]});
            skFitSpline(sketch, "E290", {"points": [v(2.04, 45.42) * mm, v(3.57, 45.16) * mm, v(5.04, 44.69) * mm, v(6.55, 44.35) * mm]});
            skFitSpline(sketch, "E291", {"points": [v(6.55, 44.35) * mm, v(8.37, 43.95) * mm, v(10.2, 43.7) * mm, v(12.06, 43.72) * mm]});
            skFitSpline(sketch, "E292", {"points": [v(12.06, 43.72) * mm, v(14.87, 43.77) * mm, v(17.47, 42.99) * mm, v(20.03, 41.9) * mm]});
            skFitSpline(sketch, "E293", {"points": [v(20.03, 41.9) * mm, v(22.15, 41) * mm, v(24.19, 39.94) * mm, v(26.08, 38.6) * mm]});
            skFitSpline(sketch, "E294", {"points": [v(26.08, 38.6) * mm, v(26.17, 38.53) * mm, v(26.25, 38.43) * mm, v(26.44, 38.49) * mm]});
            skFitSpline(sketch, "E295", {"points": [v(26.44, 38.49) * mm, v(25.56, 39.48) * mm, v(24.9, 40.61) * mm, v(24.5, 41.84) * mm]});
            skFitSpline(sketch, "E296", {"points": [v(24.5, 41.84) * mm, v(23.83, 43.93) * mm, v(23.78, 46.02) * mm, v(25.03, 47.97) * mm]});
            skFitSpline(sketch, "E297", {"points": [v(25.03, 47.97) * mm, v(25.46, 48.64) * mm, v(26.12, 49) * mm, v(26.82, 49.4) * mm]});
            skFitSpline(sketch, "E298", {"points": [v(26.82, 49.4) * mm, v(25.63, 50.1) * mm, v(24.78, 51.15) * mm, v(23.76, 52) * mm]});
            skFitSpline(sketch, "E299", {"points": [v(23.76, 52) * mm, v(22.25, 53.27) * mm, v(20.44, 53.7) * mm, v(18.55, 53.75) * mm]});
            skFitSpline(sketch, "E300", {"points": [v(18.55, 53.75) * mm, v(17.1, 53.78) * mm, v(15.64, 53.72) * mm, v(14.19, 53.67) * mm]});
            skFitSpline(sketch, "E301", {"points": [v(14.19, 53.67) * mm, v(9.06, 53.52) * mm, v(4.2, 54.58) * mm, v(-0.26, 57.24) * mm]});
            skFitSpline(sketch, "E302", {"points": [v(-0.26, 57.24) * mm, v(-2.15, 58.37) * mm, v(-4.03, 59.52) * mm, v(-6.07, 60.37) * mm]});
            skFitSpline(sketch, "E303", {"points": [v(-6.07, 60.37) * mm, v(-8.01, 61.18) * mm, v(-10.04, 61.62) * mm, v(-12.13, 61.77) * mm]});
            skFitSpline(sketch, "E304", {"points": [v(-12.13, 61.77) * mm, v(-12.45, 61.8) * mm, v(-12.78, 61.8) * mm, v(-13.07, 61.96) * mm]});
            skFitSpline(sketch, "E305", {"points": [v(-13.17, 61.96) * mm, v(-13.5, 61.88) * mm, v(-13.84, 61.88) * mm, v(-14.17, 61.96) * mm]});
            skFitSpline(sketch, "E306", {"points": [v(-42.85, 34.16) * mm, v(-42.6, 33.55) * mm, v(-42.66, 32.89) * mm, v(-42.57, 32.25) * mm]});
            skFitSpline(sketch, "E307", {"points": [v(-42.57, 32.25) * mm, v(-41.63, 25.4) * mm, v(-38.8, 19.57) * mm, v(-33.58, 15.04) * mm]});
            skFitSpline(sketch, "E308", {"points": [v(-33.58, 15.04) * mm, v(-30.64, 12.5) * mm, v(-27.24, 10.89) * mm, v(-23.4, 10.27) * mm]});
            skFitSpline(sketch, "E309", {"points": [v(-23.4, 10.27) * mm, v(-21.75, 10) * mm, v(-20.07, 10.08) * mm, v(-18.4, 10.01) * mm]});
            skFitSpline(sketch, "E310", {"points": [v(-18.4, 10.01) * mm, v(-17.32, 9.97) * mm, v(-16.24, 9.98) * mm, v(-15.16, 9.75) * mm]});
            skFitSpline(sketch, "E311", {"points": [v(-15.16, 9.75) * mm, v(-13.94, 9.5) * mm, v(-13.02, 8.84) * mm, v(-12.34, 7.82) * mm]});
            skFitSpline(sketch, "E312", {"points": [v(-12.34, 7.82) * mm, v(-12.12, 7.48) * mm, v(-11.9, 7.13) * mm, v(-11.74, 6.76) * mm]});
            skFitSpline(sketch, "E313", {"points": [v(-11.74, 6.76) * mm, v(-10.3, 3.3) * mm, v(-8.86, -0.17) * mm, v(-8.04, -3.86) * mm]});
            skFitSpline(sketch, "E314", {"points": [v(-8.04, -3.86) * mm, v(-7.85, -4.74) * mm, v(-7.75, -5.63) * mm, v(-7.8, -6.53) * mm]});
            skFitSpline(sketch, "E315", {"points": [v(-7.8, -6.53) * mm, v(-7.87, -7.98) * mm, v(-8.87, -8.66) * mm, v(-10.2, -8.17) * mm]});
            skFitSpline(sketch, "E316", {"points": [v(-10.2, -8.17) * mm, v(-10.5, -8.06) * mm, v(-10.77, -7.92) * mm, v(-11.11, -7.77) * mm]});
            skFitSpline(sketch, "E317", {"points": [v(-11.11, -7.77) * mm, v(-10.83, -8.76) * mm, v(-10.4, -9.55) * mm, v(-9.6, -10.14) * mm]});
            skFitSpline(sketch, "E318", {"points": [v(-9.6, -10.14) * mm, v(-8.24, -11.18) * mm, v(-6.68, -11.65) * mm, v(-5.02, -11.86) * mm]});
            skFitSpline(sketch, "E319", {"points": [v(-5.02, -11.86) * mm, v(-3.36, -12.08) * mm, v(-1.69, -12.11) * mm, v(-0.02, -12.17) * mm]});
            skFitSpline(sketch, "E320", {"points": [v(-0.02, -12.17) * mm, v(1.77, -12.22) * mm, v(3.54, -12.5) * mm, v(5.32, -12.72) * mm]});
            skFitSpline(sketch, "E321", {"points": [v(5.32, -12.72) * mm, v(8.35, -13.1) * mm, v(11.34, -13.75) * mm, v(14.36, -14.21) * mm]});
            skFitSpline(sketch, "E322", {"points": [v(14.36, -14.21) * mm, v(15.18, -14.34) * mm, v(15.97, -14.63) * mm, v(16.8, -14.73) * mm]});
            skFitSpline(sketch, "E323", {"points": [v(16.8, -14.73) * mm, v(16.9, -14.75) * mm, v(17.02, -14.82) * mm, v(17.01, -14.63) * mm]});
            skFitSpline(sketch, "E324", {"points": [v(17.01, -14.63) * mm, v(12.02, -12.4) * mm, v(7.75, -9.18) * mm, v(4.03, -5.13) * mm]});
            skFitSpline(sketch, "E325", {"points": [v(4.03, -5.13) * mm, v(2.16, -3.09) * mm, v(0.67, -0.8) * mm, v(-0.78, 1.53) * mm]});
            skFitSpline(sketch, "E326", {"points": [v(-0.78, 1.53) * mm, v(-4.46, 7.42) * mm, v(-6.77, 13.86) * mm, v(-8.17, 20.65) * mm]});
            skFitSpline(sketch, "E327", {"points": [v(-8.17, 20.65) * mm, v(-8.35, 21.53) * mm, v(-8.42, 22.43) * mm, v(-8.82, 23.24) * mm]});
            skFitSpline(sketch, "E328", {"points": [v(-8.82, 23.24) * mm, v(-9.7, 25.03) * mm, v(-11.2, 25.93) * mm, v(-13, 26.38) * mm]});
            skFitSpline(sketch, "E329", {"points": [v(-13, 26.38) * mm, v(-13.23, 26.44) * mm, v(-13.46, 26.48) * mm, v(-13.7, 26.5) * mm]});
            skFitSpline(sketch, "E330", {"points": [v(-13.7, 26.5) * mm, v(-14.73, 26.63) * mm, v(-15.75, 26.77) * mm, v(-16.72, 27.26) * mm]});
            skFitSpline(sketch, "E331", {"points": [v(-16.72, 27.26) * mm, v(-16.76, 26.85) * mm, v(-16.57, 26.54) * mm, v(-16.48, 26.2) * mm]});
            skFitSpline(sketch, "E332", {"points": [v(-16.48, 26.2) * mm, v(-16, 24.4) * mm, v(-15.74, 22.58) * mm, v(-16, 20.73) * mm]});
            skFitSpline(sketch, "E333", {"points": [v(-16, 20.73) * mm, v(-16.34, 18.26) * mm, v(-17.79, 16.82) * mm, v(-20.15, 16.25) * mm]});
            skFitSpline(sketch, "E334", {"points": [v(-20.15, 16.25) * mm, v(-23.4, 15.45) * mm, v(-26.44, 16.11) * mm, v(-29.3, 17.73) * mm]});
            skFitSpline(sketch, "E335", {"points": [v(-29.3, 17.73) * mm, v(-32.8, 19.7) * mm, v(-35.18, 22.74) * mm, v(-36.93, 26.32) * mm]});
            skFitSpline(sketch, "E336", {"points": [v(-36.93, 26.32) * mm, v(-38.65, 29.84) * mm, v(-39.63, 33.57) * mm, v(-39.2, 37.5) * mm]});
            skFitSpline(sketch, "E337", {"points": [v(-39.2, 37.5) * mm, v(-38.63, 42.7) * mm, v(-36.87, 47.38) * mm, v(-32.6, 50.7) * mm]});
            skFitSpline(sketch, "E338", {"points": [v(-32.6, 50.7) * mm, v(-31, 51.94) * mm, v(-29.21, 52.95) * mm, v(-27.17, 53.25) * mm]});
            skFitSpline(sketch, "E339", {"points": [v(-27.17, 53.25) * mm, v(-24.16, 53.7) * mm, v(-21.31, 53.26) * mm, v(-18.96, 51.14) * mm]});
            skFitSpline(sketch, "E340", {"points": [v(-18.96, 51.14) * mm, v(-17.44, 49.76) * mm, v(-17.08, 47.92) * mm, v(-17.36, 45.94) * mm]});
            skFitSpline(sketch, "E341", {"points": [v(-17.36, 45.94) * mm, v(-17.41, 45.6) * mm, v(-17.63, 45.32) * mm, v(-17.87, 45.07) * mm]});
            skFitSpline(sketch, "E342", {"points": [v(-17.87, 45.07) * mm, v(-18.18, 44.74) * mm, v(-18.5, 44.41) * mm, v(-18.82, 44.07) * mm]});
            skFitSpline(sketch, "E343", {"points": [v(-18.82, 44.07) * mm, v(-17.8, 43.58) * mm, v(-17.01, 42.78) * mm, v(-16.24, 41.96) * mm]});
            skFitSpline(sketch, "E344", {"points": [v(-16.24, 41.96) * mm, v(-15.3, 40.97) * mm, v(-14.34, 40.01) * mm, v(-13.2, 39.25) * mm]});
            skFitSpline(sketch, "E345", {"points": [v(-13.2, 39.25) * mm, v(-12.69, 38.9) * mm, v(-12.15, 38.94) * mm, v(-11.61, 38.96) * mm]});
            skFitSpline(sketch, "E346", {"points": [v(-11.61, 38.96) * mm, v(-11.36, 38.97) * mm, v(-11.24, 39.24) * mm, v(-11.12, 39.43) * mm]});
            skFitSpline(sketch, "E347", {"points": [v(-11.12, 39.43) * mm, v(-10.82, 39.9) * mm, v(-10.67, 40.43) * mm, v(-10.62, 40.96) * mm]});
            skFitSpline(sketch, "E348", {"points": [v(-10.62, 40.96) * mm, v(-10.29, 44.25) * mm, v(-10.66, 47.45) * mm, v(-11.87, 50.53) * mm]});
            skFitSpline(sketch, "E349", {"points": [v(-11.87, 50.53) * mm, v(-12.63, 52.45) * mm, v(-13.6, 54.26) * mm, v(-15, 55.8) * mm]});
            skFitSpline(sketch, "E350", {"points": [v(-15, 55.8) * mm, v(-16.53, 57.5) * mm, v(-18.38, 58.65) * mm, v(-20.61, 59.1) * mm]});
            skFitSpline(sketch, "E351", {"points": [v(-20.61, 59.1) * mm, v(-26.57, 60.31) * mm, v(-31.67, 58.5) * mm, v(-36.12, 54.5) * mm]});
            skFitSpline(sketch, "E352", {"points": [v(-36.12, 54.5) * mm, v(-38.56, 52.3) * mm, v(-39.83, 49.38) * mm, v(-40.94, 46.37) * mm]});
            skFitSpline(sketch, "E353", {"points": [v(-40.94, 46.37) * mm, v(-41.85, 43.9) * mm, v(-42.33, 41.33) * mm, v(-42.66, 38.73) * mm]});
            skFitSpline(sketch, "E354", {"points": [v(-42.66, 38.73) * mm, v(-42.7, 38.46) * mm, v(-42.67, 38.17) * mm, v(-42.85, 37.93) * mm]});
            skFitSpline(sketch, "E355", {"points": [v(-42.85, 36.81) * mm, v(-42.77, 36.37) * mm, v(-42.77, 35.93) * mm, v(-42.85, 35.49) * mm]});
            skFitSpline(sketch, "E356", {"points": [v(-42.85, 34.98) * mm, v(-42.8, 34.91) * mm, v(-42.8, 34.84) * mm, v(-42.85, 34.78) * mm]});
            skFitSpline(sketch, "E357", {"points": [v(40.63, -16.62) * mm, v(40.03, -16.65) * mm, v(39.42, -16.48) * mm, v(38.83, -16.7) * mm]});
            skFitSpline(sketch, "E358", {"points": [v(-42.85, 35.49) * mm, v(-42.69, 35.93) * mm, v(-42.69, 36.37) * mm, v(-42.85, 36.81) * mm]});
            skFitSpline(sketch, "E359", {"points": [v(-14.22, 61.96) * mm, v(-13.88, 61.8) * mm, v(-13.55, 61.8) * mm, v(-13.21, 61.96) * mm]});
            skFitSpline(sketch, "E360", {"points": [v(-42.85, 34.77) * mm, v(-42.7, 34.84) * mm, v(-42.72, 34.91) * mm, v(-42.85, 34.98) * mm]});
            skFitSpline(sketch, "E361", {"points": [v(36.2, -31.09) * mm, v(36.2, -31.19) * mm, v(36.14, -31.33) * mm, v(36.03, -31.52) * mm]});
            skFitSpline(sketch, "E362", {"points": [v(35.01, -30.98) * mm, v(34.51, -30.8) * mm, v(33.97, -30.7) * mm, v(33.37, -30.7) * mm]});
            skFitSpline(sketch, "E363", {"points": [v(27.52, -30.26) * mm, v(27.27, -29.84) * mm, v(27.06, -29.54) * mm, v(26.88, -29.35) * mm]});
            skFitSpline(sketch, "E364", {"points": [v(26.9, -29.28) * mm, v(26.91, -29.26) * mm, v(26.95, -29.22) * mm, v(27.02, -29.17) * mm]});
            skFitSpline(sketch, "E365", {"points": [v(27.02, -29.17) * mm, v(27.1, -29.12) * mm, v(27.16, -29.1) * mm, v(27.2, -29.1) * mm]});
            skFitSpline(sketch, "E366", {"points": [v(27.2, -29.1) * mm, v(27.32, -29.1) * mm, v(27.44, -29.17) * mm, v(27.55, -29.3) * mm]});
            skFitSpline(sketch, "E367", {"points": [v(27.55, -29.3) * mm, v(27.67, -29.44) * mm, v(27.78, -29.53) * mm, v(27.9, -29.57) * mm]});
            skFitSpline(sketch, "E368", {"points": [v(27.9, -29.57) * mm, v(28.63, -29.7) * mm, v(29.44, -29.76) * mm, v(30.32, -29.76) * mm]});
            skFitSpline(sketch, "E369", {"points": [v(34.41, -29.76) * mm, v(34.56, -29.76) * mm, v(34.8, -29.83) * mm, v(35.12, -29.97) * mm]});
            skFitSpline(sketch, "E370", {"points": [v(35.12, -29.97) * mm, v(35.46, -30.15) * mm, v(35.73, -30.31) * mm, v(35.93, -30.47) * mm]});
            skFitSpline(sketch, "E371", {"points": [v(35.93, -30.47) * mm, v(36.1, -30.6) * mm, v(36.2, -30.81) * mm, v(36.2, -31.09) * mm]});
            skFitSpline(sketch, "E372", {"points": [v(37.7, -29.32) * mm, v(38.17, -28.53) * mm, v(38.41, -27.65) * mm, v(38.41, -26.7) * mm]});
            skFitSpline(sketch, "E373", {"points": [v(38.41, -26.7) * mm, v(38.41, -26.04) * mm, v(38.22, -25.5) * mm, v(37.83, -25.09) * mm]});
            skFitSpline(sketch, "E374", {"points": [v(37.83, -25.09) * mm, v(37.44, -24.67) * mm, v(36.94, -24.4) * mm, v(36.33, -24.26) * mm]});
            skFitSpline(sketch, "E375", {"points": [v(36.33, -24.26) * mm, v(35.71, -24.13) * mm, v(34.95, -24.06) * mm, v(34.05, -24.06) * mm]});
            skFitSpline(sketch, "E376", {"points": [v(29.36, -24.3) * mm, v(28.94, -24.3) * mm, v(28.54, -24.31) * mm, v(28.15, -24.33) * mm]});
            skFitSpline(sketch, "E377", {"points": [v(28.15, -24.33) * mm, v(27.77, -24.35) * mm, v(27.48, -24.37) * mm, v(27.3, -24.39) * mm]});
            skFitSpline(sketch, "E378", {"points": [v(27.09, -23.13) * mm, v(28, -23.03) * mm, v(28.78, -22.97) * mm, v(29.45, -22.97) * mm]});
            skFitSpline(sketch, "E379", {"points": [v(36.14, -22.66) * mm, v(37.23, -22.66) * mm, v(38, -22.85) * mm, v(38.45, -23.23) * mm]});
            skFitSpline(sketch, "E380", {"points": [v(38.45, -23.23) * mm, v(38.93, -23.57) * mm, v(39.17, -24.28) * mm, v(39.17, -25.34) * mm]});
            skFitSpline(sketch, "E381", {"points": [v(39.17, -25.34) * mm, v(39.17, -26.27) * mm, v(39.07, -27.09) * mm, v(38.87, -27.8) * mm]});
            skFitSpline(sketch, "E382", {"points": [v(38.87, -27.8) * mm, v(38.67, -28.5) * mm, v(38.4, -29.07) * mm, v(38.04, -29.5) * mm]});
            skFitSpline(sketch, "E383", {"points": [v(41.6, -35.22) * mm, v(41.97, -35.64) * mm, v(42.27, -36.2) * mm, v(42.5, -36.9) * mm]});
            skFitSpline(sketch, "E384", {"points": [v(42.5, -36.9) * mm, v(42.74, -37.59) * mm, v(42.85, -38.1) * mm, v(42.85, -38.46) * mm]});
            skFitSpline(sketch, "E385", {"points": [v(42.85, -38.46) * mm, v(42.85, -39.3) * mm, v(42.5, -39.99) * mm, v(41.78, -40.53) * mm]});
            skFitSpline(sketch, "E386", {"points": [v(41.78, -40.53) * mm, v(41.06, -41.07) * mm, v(40, -41.34) * mm, v(38.6, -41.34) * mm]});
            skFitSpline(sketch, "E387", {"points": [v(38.6, -41.34) * mm, v(38.15, -41.34) * mm, v(37.7, -41.28) * mm, v(37.25, -41.15) * mm]});
            skFitSpline(sketch, "E388", {"points": [v(37.25, -41.15) * mm, v(36.8, -41.02) * mm, v(36.23, -40.79) * mm, v(35.56, -40.46) * mm]});
            skFitSpline(sketch, "E389", {"points": [v(35.56, -40.46) * mm, v(34.89, -40.13) * mm, v(34.18, -39.58) * mm, v(33.43, -38.82) * mm]});
            skFitSpline(sketch, "E390", {"points": [v(33.43, -38.82) * mm, v(32.68, -38.05) * mm, v(32.09, -37.3) * mm, v(31.65, -36.54) * mm]});
            skFitSpline(sketch, "E391", {"points": [v(31.65, -36.54) * mm, v(31.22, -35.8) * mm, v(30.9, -34.88) * mm, v(30.71, -33.8) * mm]});
            skFitSpline(sketch, "E392", {"points": [v(30.71, -33.8) * mm, v(30.52, -32.72) * mm, v(30.36, -31.52) * mm, v(30.25, -30.2) * mm]});
            skFitSpline(sketch, "E393", {"points": [v(29.88, -26.54) * mm, v(29.74, -25.38) * mm, v(29.63, -24.72) * mm, v(29.55, -24.56) * mm]});
            skFitSpline(sketch, "E394", {"points": [v(29.3, -24.3) * mm, v(29.2, -24.2) * mm, v(29.15, -24.15) * mm, v(29.13, -24.1) * mm]});
            skFitSpline(sketch, "E395", {"points": [v(29.13, -24.1) * mm, v(29.11, -24.07) * mm, v(29.1, -24.04) * mm, v(29.08, -24) * mm]});
            skFitSpline(sketch, "E396", {"points": [v(29.08, -24) * mm, v(29.12, -23.98) * mm, v(29.15, -23.96) * mm, v(29.18, -23.96) * mm]});
            skFitSpline(sketch, "E397", {"points": [v(29.55, -24.04) * mm, v(30.22, -24.23) * mm, v(30.7, -24.7) * mm, v(31.01, -25.46) * mm]});
            skFitSpline(sketch, "E398", {"points": [v(31.01, -25.46) * mm, v(31.32, -26.2) * mm, v(31.52, -26.85) * mm, v(31.61, -27.39) * mm]});
            skFitSpline(sketch, "E399", {"points": [v(31.61, -27.39) * mm, v(31.71, -27.92) * mm, v(31.76, -28.48) * mm, v(31.76, -29.06) * mm]});
            skFitSpline(sketch, "E400", {"points": [v(31.88, -31.82) * mm, v(31.88, -32.1) * mm, v(31.89, -32.36) * mm, v(31.92, -32.58) * mm]});
            skFitSpline(sketch, "E401", {"points": [v(31.92, -32.58) * mm, v(31.94, -32.8) * mm, v(32, -33.16) * mm, v(32.07, -33.64) * mm]});
            skFitSpline(sketch, "E402", {"points": [v(32.07, -33.64) * mm, v(32.15, -34.3) * mm, v(32.27, -34.99) * mm, v(32.45, -35.7) * mm]});
            skFitSpline(sketch, "E403", {"points": [v(32.45, -35.7) * mm, v(32.62, -36.42) * mm, v(32.86, -37.03) * mm, v(33.17, -37.52) * mm]});
            skFitSpline(sketch, "E404", {"points": [v(33.17, -37.52) * mm, v(33.47, -38.01) * mm, v(33.84, -38.43) * mm, v(34.26, -38.78) * mm]});
            skFitSpline(sketch, "E405", {"points": [v(34.26, -38.78) * mm, v(34.69, -39.09) * mm, v(35.16, -39.32) * mm, v(35.68, -39.48) * mm]});
            skFitSpline(sketch, "E406", {"points": [v(35.68, -39.48) * mm, v(36.2, -39.63) * mm, v(36.72, -39.71) * mm, v(37.27, -39.71) * mm]});
            skFitSpline(sketch, "E407", {"points": [v(38.3, -39.63) * mm, v(38.88, -39.54) * mm, v(39.37, -39.44) * mm, v(39.78, -39.32) * mm]});
            skFitSpline(sketch, "E408", {"points": [v(39.78, -39.32) * mm, v(40.19, -39.2) * mm, v(40.56, -39.06) * mm, v(40.88, -38.89) * mm]});
            skFitSpline(sketch, "E409", {"points": [v(40.88, -38.89) * mm, v(41.21, -38.72) * mm, v(41.47, -38.5) * mm, v(41.65, -38.22) * mm]});
            skFitSpline(sketch, "E410", {"points": [v(41.65, -38.22) * mm, v(41.83, -37.95) * mm, v(41.92, -37.64) * mm, v(41.92, -37.28) * mm]});
            skFitSpline(sketch, "E411", {"points": [v(41.92, -37.28) * mm, v(41.92, -37.03) * mm, v(41.88, -36.79) * mm, v(41.8, -36.55) * mm]});
            skFitSpline(sketch, "E412", {"points": [v(41.8, -36.55) * mm, v(41.73, -36.31) * mm, v(41.63, -36.11) * mm, v(41.52, -35.94) * mm]});
            skFitSpline(sketch, "E413", {"points": [v(41.52, -35.94) * mm, v(41.46, -35.83) * mm, v(41.42, -35.74) * mm, v(41.37, -35.68) * mm]});
            skFitSpline(sketch, "E414", {"points": [v(41.37, -35.68) * mm, v(41.32, -35.62) * mm, v(41.25, -35.53) * mm, v(41.15, -35.4) * mm]});
            skFitSpline(sketch, "E415", {"points": [v(40.72, -34.76) * mm, v(40.72, -34.65) * mm, v(40.78, -34.6) * mm, v(40.91, -34.6) * mm]});
            skFitSpline(sketch, "E416", {"points": [v(40.91, -34.6) * mm, v(41, -34.6) * mm, v(41.23, -34.8) * mm, v(41.6, -35.22) * mm]});
            skFitSpline(sketch, "E417", {"points": [v(24.15, -33.75) * mm, v(24.06, -33.18) * mm, v(23.87, -31.77) * mm, v(23.56, -29.53) * mm]});
            skFitSpline(sketch, "E418", {"points": [v(23.5, -28.89) * mm, v(23.5, -28.54) * mm, v(23.58, -28.37) * mm, v(23.75, -28.37) * mm]});
            skFitSpline(sketch, "E419", {"points": [v(23.75, -28.37) * mm, v(23.88, -28.37) * mm, v(24.04, -28.42) * mm, v(24.23, -28.54) * mm]});
            skFitSpline(sketch, "E420", {"points": [v(26.33, -30.01) * mm, v(26.43, -30.09) * mm, v(26.48, -30.19) * mm, v(26.48, -30.3) * mm]});
            skFitSpline(sketch, "E421", {"points": [v(26.17, -30.3) * mm, v(26.07, -30.28) * mm, v(25.91, -30.2) * mm, v(25.7, -30.04) * mm]});
            skFitSpline(sketch, "E422", {"points": [v(25.7, -30.04) * mm, v(25.49, -29.9) * mm, v(25.34, -29.82) * mm, v(25.26, -29.82) * mm]});
            skFitSpline(sketch, "E423", {"points": [v(25.26, -29.82) * mm, v(25.19, -29.82) * mm, v(25.15, -29.98) * mm, v(25.15, -30.3) * mm]});
            skFitSpline(sketch, "E424", {"points": [v(25.79, -35.64) * mm, v(25.8, -35.72) * mm, v(25.82, -35.8) * mm, v(25.83, -35.86) * mm]});
            skFitSpline(sketch, "E425", {"points": [v(25.83, -35.86) * mm, v(25.85, -35.93) * mm, v(25.87, -35.98) * mm, v(25.88, -36) * mm]});
            skFitSpline(sketch, "E426", {"points": [v(24.4, -35.44) * mm, v(24.32, -34.88) * mm, v(24.23, -34.32) * mm, v(24.15, -33.75) * mm]});
            skFitSpline(sketch, "E427", {"points": [v(21.46, -30.67) * mm, v(20.87, -29.75) * mm, v(20.57, -29.17) * mm, v(20.57, -28.93) * mm]});
            skFitSpline(sketch, "E428", {"points": [v(20.57, -28.93) * mm, v(20.57, -28.55) * mm, v(20.73, -28.37) * mm, v(21.05, -28.37) * mm]});
            skFitSpline(sketch, "E429", {"points": [v(21.05, -28.37) * mm, v(21.3, -28.37) * mm, v(21.63, -28.5) * mm, v(22.03, -28.76) * mm]});
            skFitSpline(sketch, "E430", {"points": [v(22.03, -28.76) * mm, v(22.44, -29.03) * mm, v(22.83, -29.4) * mm, v(23.19, -29.85) * mm]});
            skFitSpline(sketch, "E431", {"points": [v(23.89, -30.75) * mm, v(24.12, -30.85) * mm, v(24.23, -31.02) * mm, v(24.23, -31.25) * mm]});
            skFitSpline(sketch, "E432", {"points": [v(24.23, -31.25) * mm, v(24.23, -31.3) * mm, v(24.2, -31.35) * mm, v(24.14, -31.4) * mm]});
            skFitSpline(sketch, "E433", {"points": [v(24.14, -31.4) * mm, v(24.03, -31.4) * mm, v(23.87, -31.33) * mm, v(23.65, -31.18) * mm]});
            skFitSpline(sketch, "E434", {"points": [v(23.19, -30.77) * mm, v(22.74, -30.3) * mm, v(22.42, -30.07) * mm, v(22.24, -30.07) * mm]});
            skFitSpline(sketch, "E435", {"points": [v(22.24, -30.07) * mm, v(22.15, -30.07) * mm, v(22.1, -30.14) * mm, v(22.1, -30.27) * mm]});
            skFitSpline(sketch, "E436", {"points": [v(22.1, -30.27) * mm, v(22.1, -30.43) * mm, v(22.16, -30.68) * mm, v(22.27, -31) * mm]});
            skFitSpline(sketch, "E437", {"points": [v(22.27, -31) * mm, v(22.38, -31.33) * mm, v(22.44, -31.56) * mm, v(22.47, -31.7) * mm]});
            skFitSpline(sketch, "E438", {"points": [v(22.47, -31.7) * mm, v(22.5, -31.84) * mm, v(22.52, -31.96) * mm, v(22.53, -32.05) * mm]});
            skFitSpline(sketch, "E439", {"points": [v(22.53, -32.05) * mm, v(22.41, -32.05) * mm, v(22.06, -31.59) * mm, v(21.46, -30.67) * mm]});
            skFitSpline(sketch, "E440", {"points": [v(15.02, -29.33) * mm, v(14.92, -29.28) * mm, v(14.83, -29.19) * mm, v(14.76, -29.06) * mm]});
            skFitSpline(sketch, "E441", {"points": [v(14.76, -29.06) * mm, v(14.7, -28.94) * mm, v(14.65, -28.82) * mm, v(14.65, -28.72) * mm]});
            skFitSpline(sketch, "E442", {"points": [v(14.65, -28.72) * mm, v(14.65, -28.52) * mm, v(14.85, -28.42) * mm, v(15.24, -28.42) * mm]});
            skFitSpline(sketch, "E443", {"points": [v(16.71, -28.55) * mm, v(17.06, -28.55) * mm, v(17.39, -28.64) * mm, v(17.7, -28.8) * mm]});
            skFitSpline(sketch, "E444", {"points": [v(17.7, -28.8) * mm, v(18, -28.96) * mm, v(18.35, -29.24) * mm, v(18.73, -29.65) * mm]});
            skFitSpline(sketch, "E445", {"points": [v(18.73, -29.65) * mm, v(19.1, -30.06) * mm, v(19.4, -30.54) * mm, v(19.6, -31.09) * mm]});
            skFitSpline(sketch, "E446", {"points": [v(19.6, -31.09) * mm, v(19.8, -31.63) * mm, v(19.96, -32.08) * mm, v(20.05, -32.43) * mm]});
            skFitSpline(sketch, "E447", {"points": [v(20.05, -32.43) * mm, v(20.14, -32.78) * mm, v(20.2, -33.1) * mm, v(20.25, -33.38) * mm]});
            skFitSpline(sketch, "E448", {"points": [v(20.25, -33.38) * mm, v(20.3, -33.67) * mm, v(20.32, -33.9) * mm, v(20.34, -34.1) * mm]});
            skFitSpline(sketch, "E449", {"points": [v(20.34, -34.1) * mm, v(20.35, -34.28) * mm, v(20.36, -34.42) * mm, v(20.36, -34.5) * mm]});
            skFitSpline(sketch, "E450", {"points": [v(20.36, -34.5) * mm, v(20.36, -35.53) * mm, v(20.07, -36.04) * mm, v(19.5, -36.04) * mm]});
            skFitSpline(sketch, "E451", {"points": [v(19.5, -36.04) * mm, v(18.97, -36.04) * mm, v(18.24, -35.55) * mm, v(17.3, -34.56) * mm]});
            skFitSpline(sketch, "E452", {"points": [v(16.63, -33.84) * mm, v(16.43, -33.63) * mm, v(16.26, -33.42) * mm, v(16.13, -33.2) * mm]});
            skFitSpline(sketch, "E453", {"points": [v(16.13, -33.2) * mm, v(16, -32.97) * mm, v(15.93, -32.75) * mm, v(15.93, -32.53) * mm]});
            skFitSpline(sketch, "E454", {"points": [v(15.93, -32.53) * mm, v(15.93, -32.47) * mm, v(15.96, -32.39) * mm, v(16.01, -32.3) * mm]});
            skFitSpline(sketch, "E455", {"points": [v(16.46, -32.84) * mm, v(16.73, -33.22) * mm, v(17.05, -33.61) * mm, v(17.43, -34) * mm]});
            skFitSpline(sketch, "E456", {"points": [v(17.43, -34) * mm, v(17.8, -34.4) * mm, v(18.13, -34.6) * mm, v(18.4, -34.6) * mm]});
            skFitSpline(sketch, "E457", {"points": [v(18.4, -34.6) * mm, v(18.72, -34.6) * mm, v(18.88, -34.26) * mm, v(18.88, -33.58) * mm]});
            skFitSpline(sketch, "E458", {"points": [v(18.88, -33.58) * mm, v(18.88, -33.1) * mm, v(18.81, -32.5) * mm, v(18.68, -31.8) * mm]});
            skFitSpline(sketch, "E459", {"points": [v(18.68, -31.8) * mm, v(18.54, -31.1) * mm, v(18.39, -30.58) * mm, v(18.21, -30.24) * mm]});
            skFitSpline(sketch, "E460", {"points": [v(18.21, -30.24) * mm, v(18.04, -29.9) * mm, v(17.85, -29.68) * mm, v(17.65, -29.57) * mm]});
            skFitSpline(sketch, "E461", {"points": [v(17.65, -29.57) * mm, v(17.45, -29.46) * mm, v(17.22, -29.4) * mm, v(16.96, -29.4) * mm]});
            skFitSpline(sketch, "E462", {"points": [v(14.54, -29.14) * mm, v(14.54, -28.69) * mm, v(14.68, -28.46) * mm, v(14.97, -28.46) * mm]});
            skFitSpline(sketch, "E463", {"points": [v(14.97, -28.46) * mm, v(15.12, -28.46) * mm, v(15.3, -28.55) * mm, v(15.53, -28.73) * mm]});
            skFitSpline(sketch, "E464", {"points": [v(15.53, -28.73) * mm, v(15.72, -28.93) * mm, v(15.88, -29.18) * mm, v(16, -29.48) * mm]});
            skFitSpline(sketch, "E465", {"points": [v(16, -29.48) * mm, v(16.12, -29.78) * mm, v(16.2, -30.05) * mm, v(16.26, -30.28) * mm]});
            skFitSpline(sketch, "E466", {"points": [v(16.26, -30.28) * mm, v(16.31, -30.5) * mm, v(16.35, -30.78) * mm, v(16.38, -31.1) * mm]});
            skFitSpline(sketch, "E467", {"points": [v(16.85, -35.3) * mm, v(16.85, -35.79) * mm, v(16.74, -36.03) * mm, v(16.52, -36.03) * mm]});
            skFitSpline(sketch, "E468", {"points": [v(16.52, -36.03) * mm, v(16.3, -36.03) * mm, v(16.02, -35.88) * mm, v(15.66, -35.6) * mm]});
            skFitSpline(sketch, "E469", {"points": [v(15.66, -35.6) * mm, v(15.3, -35.35) * mm, v(14.71, -34.87) * mm, v(13.9, -34.14) * mm]});
            skFitSpline(sketch, "E470", {"points": [v(13.9, -34.14) * mm, v(13.85, -34.08) * mm, v(13.8, -34.03) * mm, v(13.78, -33.99) * mm]});
            skFitSpline(sketch, "E471", {"points": [v(13.78, -33.99) * mm, v(13.76, -33.95) * mm, v(13.74, -33.91) * mm, v(13.72, -33.87) * mm]});
            skFitSpline(sketch, "E472", {"points": [v(13.72, -33.87) * mm, v(13.72, -33.85) * mm, v(13.76, -33.81) * mm, v(13.82, -33.78) * mm]});
            skFitSpline(sketch, "E473", {"points": [v(13.82, -33.78) * mm, v(13.91, -33.78) * mm, v(14.02, -33.82) * mm, v(14.16, -33.91) * mm]});
            skFitSpline(sketch, "E474", {"points": [v(14.16, -33.91) * mm, v(14.3, -34) * mm, v(14.42, -34.1) * mm, v(14.54, -34.18) * mm]});
            skFitSpline(sketch, "E475", {"points": [v(14.54, -34.18) * mm, v(14.65, -34.27) * mm, v(14.76, -34.36) * mm, v(14.85, -34.45) * mm]});
            skFitSpline(sketch, "E476", {"points": [v(15.26, -34.75) * mm, v(15.27, -34.73) * mm, v(15.28, -34.71) * mm, v(15.3, -34.68) * mm]});
            skFitSpline(sketch, "E477", {"points": [v(15.3, -34.68) * mm, v(15.32, -34.65) * mm, v(15.33, -34.6) * mm, v(15.33, -34.51) * mm]});
            skFitSpline(sketch, "E478", {"points": [v(8.27, -29.31) * mm, v(8.17, -29.25) * mm, v(8.1, -29.17) * mm, v(8.04, -29.08) * mm]});
            skFitSpline(sketch, "E479", {"points": [v(7.89, -28.74) * mm, v(7.89, -28.55) * mm, v(8.08, -28.46) * mm, v(8.47, -28.35) * mm]});
            skFitSpline(sketch, "E480", {"points": [v(10.14, -28.6) * mm, v(10.8, -28.66) * mm, v(11.4, -28.9) * mm, v(11.9, -29.32) * mm]});
            skFitSpline(sketch, "E481", {"points": [v(11.9, -29.32) * mm, v(12.39, -29.73) * mm, v(12.8, -30.26) * mm, v(13.12, -30.9) * mm]});
            skFitSpline(sketch, "E482", {"points": [v(13.12, -30.9) * mm, v(13.45, -31.53) * mm, v(13.66, -32.18) * mm, v(13.76, -32.84) * mm]});
            skFitSpline(sketch, "E483", {"points": [v(13.76, -32.84) * mm, v(13.87, -33.5) * mm, v(13.92, -34.06) * mm, v(13.92, -34.53) * mm]});
            skFitSpline(sketch, "E484", {"points": [v(13.92, -34.53) * mm, v(13.92, -35.58) * mm, v(13.67, -36.1) * mm, v(13.16, -36.1) * mm]});
            skFitSpline(sketch, "E485", {"points": [v(13.16, -36.1) * mm, v(12.73, -36.1) * mm, v(12.1, -35.65) * mm, v(11.28, -34.74) * mm]});
            skFitSpline(sketch, "E486", {"points": [v(10.47, -33.88) * mm, v(10.2, -33.6) * mm, v(10.01, -33.4) * mm, v(9.88, -33.26) * mm]});
            skFitSpline(sketch, "E487", {"points": [v(9.88, -33.26) * mm, v(9.75, -33.12) * mm, v(9.62, -32.94) * mm, v(9.49, -32.74) * mm]});
            skFitSpline(sketch, "E488", {"points": [v(9.49, -32.74) * mm, v(9.35, -32.54) * mm, v(9.28, -32.33) * mm, v(9.28, -32.1) * mm]});
            skFitSpline(sketch, "E489", {"points": [v(9.28, -32.1) * mm, v(9.28, -31.93) * mm, v(9.32, -31.84) * mm, v(9.4, -31.84) * mm]});
            skFitSpline(sketch, "E490", {"points": [v(9.4, -31.84) * mm, v(9.48, -31.84) * mm, v(9.57, -31.9) * mm, v(9.69, -32.05) * mm]});
            skFitSpline(sketch, "E491", {"points": [v(11.14, -33.94) * mm, v(11.65, -34.48) * mm, v(12.02, -34.75) * mm, v(12.27, -34.75) * mm]});
            skFitSpline(sketch, "E492", {"points": [v(12.27, -34.75) * mm, v(12.49, -34.75) * mm, v(12.6, -34.54) * mm, v(12.6, -34.13) * mm]});
            skFitSpline(sketch, "E493", {"points": [v(12.13, -31.6) * mm, v(12.02, -31.02) * mm, v(11.87, -30.55) * mm, v(11.68, -30.21) * mm]});
            skFitSpline(sketch, "E494", {"points": [v(11.68, -30.21) * mm, v(11.5, -29.87) * mm, v(11.29, -29.65) * mm, v(11.07, -29.55) * mm]});
            skFitSpline(sketch, "E495", {"points": [v(11.07, -29.55) * mm, v(10.85, -29.44) * mm, v(10.6, -29.4) * mm, v(10.33, -29.4) * mm]});
            skFitSpline(sketch, "E496", {"points": [v(8.7, -28.7) * mm, v(8.82, -28.7) * mm, v(8.99, -28.7) * mm, v(9.2, -28.7) * mm]});
            skFitSpline(sketch, "E497", {"points": [v(9.2, -28.7) * mm, v(9.37, -28.7) * mm, v(9.46, -28.75) * mm, v(9.46, -28.84) * mm]});
            skFitSpline(sketch, "E498", {"points": [v(10.47, -37.68) * mm, v(10.47, -38.03) * mm, v(10.49, -38.32) * mm, v(10.52, -38.56) * mm]});
            skFitSpline(sketch, "E499", {"points": [v(10.52, -38.56) * mm, v(10.56, -38.8) * mm, v(10.61, -39.05) * mm, v(10.68, -39.3) * mm]});
            skFitSpline(sketch, "E500", {"points": [v(10.68, -39.3) * mm, v(10.78, -39.59) * mm, v(10.95, -39.8) * mm, v(11.18, -39.95) * mm]});
            skFitSpline(sketch, "E501", {"points": [v(11.18, -39.95) * mm, v(11.44, -40.14) * mm, v(11.82, -40.24) * mm, v(12.3, -40.24) * mm]});
            skFitSpline(sketch, "E502", {"points": [v(12.3, -40.24) * mm, v(12.8, -40.24) * mm, v(13.23, -40.1) * mm, v(13.6, -39.8) * mm]});
            skFitSpline(sketch, "E503", {"points": [v(13.6, -39.8) * mm, v(13.97, -39.51) * mm, v(14.15, -39.17) * mm, v(14.15, -38.79) * mm]});
            skFitSpline(sketch, "E504", {"points": [v(14.15, -38.79) * mm, v(14.15, -38.63) * mm, v(14.09, -38.42) * mm, v(13.97, -38.16) * mm]});
            skFitSpline(sketch, "E505", {"points": [v(13.97, -38.16) * mm, v(13.84, -37.9) * mm, v(13.64, -37.65) * mm, v(13.36, -37.43) * mm]});
            skFitSpline(sketch, "E506", {"points": [v(13.36, -37.43) * mm, v(13.09, -37.2) * mm, v(12.88, -37.06) * mm, v(12.75, -36.97) * mm]});
            skFitSpline(sketch, "E507", {"points": [v(12.75, -36.97) * mm, v(12.63, -36.89) * mm, v(12.46, -36.8) * mm, v(12.25, -36.7) * mm]});
            skFitSpline(sketch, "E508", {"points": [v(11.22, -36.28) * mm, v(11.05, -36.22) * mm, v(10.93, -36.17) * mm, v(10.85, -36.13) * mm]});
            skFitSpline(sketch, "E509", {"points": [v(10.85, -36.13) * mm, v(10.78, -36.1) * mm, v(10.71, -36.05) * mm, v(10.66, -36) * mm]});
            skFitSpline(sketch, "E510", {"points": [v(10.7, -35.94) * mm, v(10.92, -35.94) * mm, v(11.3, -36.06) * mm, v(11.84, -36.3) * mm]});
            skFitSpline(sketch, "E511", {"points": [v(11.84, -36.3) * mm, v(12.39, -36.55) * mm, v(12.92, -36.85) * mm, v(13.44, -37.22) * mm]});
            skFitSpline(sketch, "E512", {"points": [v(13.44, -37.22) * mm, v(13.97, -37.58) * mm, v(14.33, -37.93) * mm, v(14.53, -38.26) * mm]});
            skFitSpline(sketch, "E513", {"points": [v(14.53, -38.26) * mm, v(14.73, -38.6) * mm, v(14.83, -39.01) * mm, v(14.83, -39.5) * mm]});
            skFitSpline(sketch, "E514", {"points": [v(14.83, -39.5) * mm, v(14.83, -40) * mm, v(14.68, -40.42) * mm, v(14.4, -40.78) * mm]});
            skFitSpline(sketch, "E515", {"points": [v(14.4, -40.78) * mm, v(14.1, -41.15) * mm, v(13.7, -41.33) * mm, v(13.16, -41.33) * mm]});
            skFitSpline(sketch, "E516", {"points": [v(13.16, -41.33) * mm, v(12.49, -41.33) * mm, v(11.78, -41.05) * mm, v(11.02, -40.5) * mm]});
            skFitSpline(sketch, "E517", {"points": [v(11.02, -40.5) * mm, v(10.26, -39.94) * mm, v(9.75, -39.25) * mm, v(9.49, -38.43) * mm]});
            skFitSpline(sketch, "E518", {"points": [v(9.49, -38.43) * mm, v(9.22, -37.6) * mm, v(9.02, -36.56) * mm, v(8.88, -35.3) * mm]});
            skFitSpline(sketch, "E519", {"points": [v(8.5, -31.75) * mm, v(8.4, -30.62) * mm, v(8.24, -29.7) * mm, v(8.04, -28.95) * mm]});
            skFitSpline(sketch, "E520", {"points": [v(8.04, -28.95) * mm, v(8.04, -28.79) * mm, v(8.26, -28.7) * mm, v(8.7, -28.7) * mm]});
            skFitSpline(sketch, "E521", {"points": [v(2.67, -29.33) * mm, v(2.57, -29.28) * mm, v(2.48, -29.19) * mm, v(2.4, -29.06) * mm]});
            skFitSpline(sketch, "E522", {"points": [v(2.4, -29.06) * mm, v(2.34, -28.94) * mm, v(2.3, -28.82) * mm, v(2.3, -28.72) * mm]});
            skFitSpline(sketch, "E523", {"points": [v(2.3, -28.72) * mm, v(2.3, -28.52) * mm, v(2.5, -28.42) * mm, v(2.88, -28.42) * mm]});
            skFitSpline(sketch, "E524", {"points": [v(4.36, -28.55) * mm, v(4.7, -28.55) * mm, v(5.04, -28.64) * mm, v(5.35, -28.8) * mm]});
            skFitSpline(sketch, "E525", {"points": [v(5.35, -28.8) * mm, v(5.66, -28.96) * mm, v(6, -29.24) * mm, v(6.37, -29.65) * mm]});
            skFitSpline(sketch, "E526", {"points": [v(6.37, -29.65) * mm, v(6.75, -30.06) * mm, v(7.04, -30.54) * mm, v(7.25, -31.09) * mm]});
            skFitSpline(sketch, "E527", {"points": [v(7.25, -31.09) * mm, v(7.45, -31.63) * mm, v(7.6, -32.08) * mm, v(7.7, -32.43) * mm]});
            skFitSpline(sketch, "E528", {"points": [v(7.7, -32.43) * mm, v(7.78, -32.78) * mm, v(7.85, -33.1) * mm, v(7.9, -33.38) * mm]});
            skFitSpline(sketch, "E529", {"points": [v(7.9, -33.38) * mm, v(7.94, -33.67) * mm, v(7.97, -33.9) * mm, v(7.98, -34.1) * mm]});
            skFitSpline(sketch, "E530", {"points": [v(7.98, -34.1) * mm, v(8, -34.28) * mm, v(8, -34.42) * mm, v(8, -34.5) * mm]});
            skFitSpline(sketch, "E531", {"points": [v(8, -34.5) * mm, v(8, -35.53) * mm, v(7.72, -36.04) * mm, v(7.15, -36.04) * mm]});
            skFitSpline(sketch, "E532", {"points": [v(7.15, -36.04) * mm, v(6.62, -36.04) * mm, v(5.88, -35.55) * mm, v(4.94, -34.56) * mm]});
            skFitSpline(sketch, "E533", {"points": [v(4.28, -33.84) * mm, v(4.07, -33.63) * mm, v(3.9, -33.42) * mm, v(3.78, -33.2) * mm]});
            skFitSpline(sketch, "E534", {"points": [v(3.78, -33.2) * mm, v(3.65, -32.97) * mm, v(3.58, -32.75) * mm, v(3.58, -32.53) * mm]});
            skFitSpline(sketch, "E535", {"points": [v(3.58, -32.53) * mm, v(3.58, -32.47) * mm, v(3.6, -32.39) * mm, v(3.66, -32.3) * mm]});
            skFitSpline(sketch, "E536", {"points": [v(4.1, -32.84) * mm, v(4.38, -33.22) * mm, v(4.7, -33.61) * mm, v(5.07, -34) * mm]});
            skFitSpline(sketch, "E537", {"points": [v(5.07, -34) * mm, v(5.45, -34.4) * mm, v(5.77, -34.6) * mm, v(6.04, -34.6) * mm]});
            skFitSpline(sketch, "E538", {"points": [v(6.04, -34.6) * mm, v(6.37, -34.6) * mm, v(6.53, -34.26) * mm, v(6.53, -33.58) * mm]});
            skFitSpline(sketch, "E539", {"points": [v(6.53, -33.58) * mm, v(6.53, -33.1) * mm, v(6.46, -32.5) * mm, v(6.33, -31.8) * mm]});
            skFitSpline(sketch, "E540", {"points": [v(6.33, -31.8) * mm, v(6.19, -31.1) * mm, v(6.03, -30.58) * mm, v(5.86, -30.24) * mm]});
            skFitSpline(sketch, "E541", {"points": [v(5.86, -30.24) * mm, v(5.69, -29.9) * mm, v(5.5, -29.68) * mm, v(5.3, -29.57) * mm]});
            skFitSpline(sketch, "E542", {"points": [v(5.3, -29.57) * mm, v(5.1, -29.46) * mm, v(4.87, -29.4) * mm, v(4.6, -29.4) * mm]});
            skFitSpline(sketch, "E543", {"points": [v(2.19, -29.14) * mm, v(2.19, -28.69) * mm, v(2.33, -28.46) * mm, v(2.62, -28.46) * mm]});
            skFitSpline(sketch, "E544", {"points": [v(2.62, -28.46) * mm, v(2.77, -28.46) * mm, v(2.96, -28.55) * mm, v(3.17, -28.73) * mm]});
            skFitSpline(sketch, "E545", {"points": [v(3.17, -28.73) * mm, v(3.37, -28.93) * mm, v(3.52, -29.18) * mm, v(3.65, -29.48) * mm]});
            skFitSpline(sketch, "E546", {"points": [v(3.65, -29.48) * mm, v(3.77, -29.78) * mm, v(3.86, -30.05) * mm, v(3.9, -30.28) * mm]});
            skFitSpline(sketch, "E547", {"points": [v(3.9, -30.28) * mm, v(3.96, -30.5) * mm, v(4, -30.78) * mm, v(4.02, -31.1) * mm]});
            skFitSpline(sketch, "E548", {"points": [v(4.5, -35.3) * mm, v(4.5, -35.79) * mm, v(4.38, -36.03) * mm, v(4.16, -36.03) * mm]});
            skFitSpline(sketch, "E549", {"points": [v(4.16, -36.03) * mm, v(3.96, -36.03) * mm, v(3.67, -35.88) * mm, v(3.3, -35.6) * mm]});
            skFitSpline(sketch, "E550", {"points": [v(3.3, -35.6) * mm, v(2.95, -35.35) * mm, v(2.36, -34.87) * mm, v(1.54, -34.14) * mm]});
            skFitSpline(sketch, "E551", {"points": [v(1.54, -34.14) * mm, v(1.5, -34.08) * mm, v(1.45, -34.03) * mm, v(1.43, -33.99) * mm]});
            skFitSpline(sketch, "E552", {"points": [v(1.43, -33.99) * mm, v(1.4, -33.95) * mm, v(1.38, -33.91) * mm, v(1.37, -33.87) * mm]});
            skFitSpline(sketch, "E553", {"points": [v(1.37, -33.87) * mm, v(1.37, -33.85) * mm, v(1.4, -33.81) * mm, v(1.47, -33.78) * mm]});
            skFitSpline(sketch, "E554", {"points": [v(1.47, -33.78) * mm, v(1.56, -33.78) * mm, v(1.67, -33.82) * mm, v(1.8, -33.91) * mm]});
            skFitSpline(sketch, "E555", {"points": [v(1.8, -33.91) * mm, v(1.94, -34) * mm, v(2.07, -34.1) * mm, v(2.18, -34.18) * mm]});
            skFitSpline(sketch, "E556", {"points": [v(2.18, -34.18) * mm, v(2.3, -34.27) * mm, v(2.4, -34.36) * mm, v(2.5, -34.45) * mm]});
            skFitSpline(sketch, "E557", {"points": [v(2.9, -34.75) * mm, v(2.92, -34.73) * mm, v(2.93, -34.71) * mm, v(2.95, -34.68) * mm]});
            skFitSpline(sketch, "E558", {"points": [v(2.95, -34.68) * mm, v(2.97, -34.65) * mm, v(2.98, -34.6) * mm, v(2.98, -34.51) * mm]});
            skFitSpline(sketch, "E559", {"points": [v(0.84, -30.58) * mm, v(0.58, -30.28) * mm, v(0.36, -30.13) * mm, v(0.17, -30.13) * mm]});
            skFitSpline(sketch, "E560", {"points": [v(0.17, -30.13) * mm, v(0.01, -30.13) * mm, v(-0.07, -30.34) * mm, v(-0.07, -30.77) * mm]});
            skFitSpline(sketch, "E561", {"points": [v(0.85, -37.11) * mm, v(1.16, -38.88) * mm, v(1.31, -40.07) * mm, v(1.31, -40.66) * mm]});
            skFitSpline(sketch, "E562", {"points": [v(1.31, -40.66) * mm, v(1.31, -41.15) * mm, v(1.2, -41.4) * mm, v(0.96, -41.4) * mm]});
            skFitSpline(sketch, "E563", {"points": [v(0.32, -41.16) * mm, v(0.12, -41.06) * mm, v(-0.05, -40.98) * mm, v(-0.17, -40.93) * mm]});
            skFitSpline(sketch, "E564", {"points": [v(-0.17, -40.93) * mm, v(-0.3, -40.88) * mm, v(-0.44, -40.82) * mm, v(-0.6, -40.76) * mm]});
            skFitSpline(sketch, "E565", {"points": [v(-0.6, -40.76) * mm, v(-0.78, -40.7) * mm, v(-1.03, -40.66) * mm, v(-1.36, -40.66) * mm]});
            skFitSpline(sketch, "E566", {"points": [v(-1.36, -40.66) * mm, v(-1.61, -40.66) * mm, v(-1.73, -40.49) * mm, v(-1.73, -40.14) * mm]});
            skFitSpline(sketch, "E567", {"points": [v(-1.73, -40.14) * mm, v(-1.73, -39.9) * mm, v(-1.62, -39.79) * mm, v(-1.4, -39.79) * mm]});
            skFitSpline(sketch, "E568", {"points": [v(-1.4, -39.79) * mm, v(-1, -40.03) * mm, v(-0.75, -40.16) * mm, v(-0.65, -40.16) * mm]});
            skFitSpline(sketch, "E569", {"points": [v(-0.65, -40.16) * mm, v(-0.5, -40.16) * mm, v(-0.43, -40) * mm, v(-0.43, -39.67) * mm]});
            skFitSpline(sketch, "E570", {"points": [v(-1.62, -29.37) * mm, v(-1.62, -28.8) * mm, v(-1.5, -28.52) * mm, v(-1.25, -28.52) * mm]});
            skFitSpline(sketch, "E571", {"points": [v(-1.25, -28.52) * mm, v(-0.9, -28.52) * mm, v(-0.36, -28.87) * mm, v(0.38, -29.58) * mm]});
            skFitSpline(sketch, "E572", {"points": [v(0.38, -29.58) * mm, v(1.12, -30.28) * mm, v(1.49, -30.7) * mm, v(1.49, -30.85) * mm]});
            skFitSpline(sketch, "E573", {"points": [v(1.49, -30.85) * mm, v(1.49, -30.96) * mm, v(1.44, -31.02) * mm, v(1.35, -31.02) * mm]});
            skFitSpline(sketch, "E574", {"points": [v(1.35, -31.02) * mm, v(1.26, -31.02) * mm, v(1.09, -30.87) * mm, v(0.84, -30.58) * mm]});
            skFitSpline(sketch, "E575", {"points": [v(-0.94, -35.28) * mm, v(-0.83, -35.19) * mm, v(-0.72, -35.14) * mm, v(-0.6, -35.14) * mm]});
            skFitSpline(sketch, "E576", {"points": [v(-0.6, -35.14) * mm, v(-0.53, -35.15) * mm, v(-0.48, -35.19) * mm, v(-0.45, -35.24) * mm]});
            skFitSpline(sketch, "E577", {"points": [v(-0.45, -35.24) * mm, v(-0.43, -35.3) * mm, v(-0.41, -35.36) * mm, v(-0.41, -35.45) * mm]});
            skFitSpline(sketch, "E578", {"points": [v(-0.36, -35.65) * mm, v(-0.24, -35.85) * mm, v(-0.18, -36) * mm, v(-0.18, -36.1) * mm]});
            skFitSpline(sketch, "E579", {"points": [v(-2.27, -36.11) * mm, v(-3.28, -36.11) * mm, v(-3.98, -35.64) * mm, v(-4.35, -34.7) * mm]});
            skFitSpline(sketch, "E580", {"points": [v(-4.35, -34.7) * mm, v(-4.72, -33.76) * mm, v(-4.97, -32.87) * mm, v(-5.1, -32.03) * mm]});
            skFitSpline(sketch, "E581", {"points": [v(-5.1, -32.03) * mm, v(-5.24, -31.2) * mm, v(-5.3, -30.66) * mm, v(-5.32, -30.45) * mm]});
            skFitSpline(sketch, "E582", {"points": [v(-5.32, -30.45) * mm, v(-5.33, -30.24) * mm, v(-5.34, -30.04) * mm, v(-5.34, -29.84) * mm]});
            skFitSpline(sketch, "E583", {"points": [v(-5.34, -29.84) * mm, v(-5.34, -28.94) * mm, v(-5.11, -28.49) * mm, v(-4.66, -28.49) * mm]});
            skFitSpline(sketch, "E584", {"points": [v(-4.66, -28.49) * mm, v(-4.2, -28.49) * mm, v(-3.5, -29) * mm, v(-2.53, -30.03) * mm]});
            skFitSpline(sketch, "E585", {"points": [v(-1.85, -30.67) * mm, v(-1.51, -30.98) * mm, v(-1.27, -31.23) * mm, v(-1.13, -31.41) * mm]});
            skFitSpline(sketch, "E586", {"points": [v(-1.13, -31.41) * mm, v(-0.99, -31.6) * mm, v(-0.92, -31.79) * mm, v(-0.92, -32) * mm]});
            skFitSpline(sketch, "E587", {"points": [v(-0.92, -32) * mm, v(-0.92, -32.05) * mm, v(-0.95, -32.1) * mm, v(-1.02, -32.17) * mm]});
            skFitSpline(sketch, "E588", {"points": [v(-1.02, -32.17) * mm, v(-1.18, -32.17) * mm, v(-1.58, -31.8) * mm, v(-2.22, -31.05) * mm]});
            skFitSpline(sketch, "E589", {"points": [v(-2.22, -31.05) * mm, v(-2.76, -30.47) * mm, v(-3.17, -30.18) * mm, v(-3.44, -30.18) * mm]});
            skFitSpline(sketch, "E590", {"points": [v(-3.44, -30.18) * mm, v(-3.72, -30.18) * mm, v(-3.87, -30.47) * mm, v(-3.87, -31.07) * mm]});
            skFitSpline(sketch, "E591", {"points": [v(-3.87, -31.07) * mm, v(-3.87, -31.6) * mm, v(-3.78, -32.28) * mm, v(-3.6, -33.1) * mm]});
            skFitSpline(sketch, "E592", {"points": [v(-3.6, -33.1) * mm, v(-3.43, -33.93) * mm, v(-3.2, -34.56) * mm, v(-2.94, -35) * mm]});
            skFitSpline(sketch, "E593", {"points": [v(-2.94, -35) * mm, v(-2.68, -35.43) * mm, v(-2.37, -35.65) * mm, v(-2, -35.65) * mm]});
            skFitSpline(sketch, "E594", {"points": [v(-2, -35.65) * mm, v(-1.7, -35.65) * mm, v(-1.34, -35.52) * mm, v(-0.94, -35.28) * mm]});
            skFitSpline(sketch, "E595", {"points": [v(-10.8, -29.33) * mm, v(-10.91, -29.28) * mm, v(-11, -29.19) * mm, v(-11.07, -29.06) * mm]});
            skFitSpline(sketch, "E596", {"points": [v(-11.07, -29.06) * mm, v(-11.14, -28.94) * mm, v(-11.18, -28.82) * mm, v(-11.18, -28.72) * mm]});
            skFitSpline(sketch, "E597", {"points": [v(-11.18, -28.72) * mm, v(-11.18, -28.52) * mm, v(-10.98, -28.42) * mm, v(-10.6, -28.42) * mm]});
            skFitSpline(sketch, "E598", {"points": [v(-9.12, -28.55) * mm, v(-8.77, -28.55) * mm, v(-8.44, -28.64) * mm, v(-8.13, -28.8) * mm]});
            skFitSpline(sketch, "E599", {"points": [v(-8.13, -28.8) * mm, v(-7.82, -28.96) * mm, v(-7.48, -29.24) * mm, v(-7.1, -29.65) * mm]});
            skFitSpline(sketch, "E600", {"points": [v(-7.1, -29.65) * mm, v(-6.73, -30.06) * mm, v(-6.44, -30.54) * mm, v(-6.23, -31.09) * mm]});
            skFitSpline(sketch, "E601", {"points": [v(-6.23, -31.09) * mm, v(-6.03, -31.63) * mm, v(-5.88, -32.08) * mm, v(-5.79, -32.43) * mm]});
            skFitSpline(sketch, "E602", {"points": [v(-5.79, -32.43) * mm, v(-5.7, -32.78) * mm, v(-5.63, -33.1) * mm, v(-5.58, -33.38) * mm]});
            skFitSpline(sketch, "E603", {"points": [v(-5.58, -33.38) * mm, v(-5.54, -33.67) * mm, v(-5.5, -33.9) * mm, v(-5.5, -34.1) * mm]});
            skFitSpline(sketch, "E604", {"points": [v(-5.5, -34.1) * mm, v(-5.48, -34.28) * mm, v(-5.48, -34.42) * mm, v(-5.48, -34.5) * mm]});
            skFitSpline(sketch, "E605", {"points": [v(-5.48, -34.5) * mm, v(-5.48, -35.53) * mm, v(-5.76, -36.04) * mm, v(-6.33, -36.04) * mm]});
            skFitSpline(sketch, "E606", {"points": [v(-6.33, -36.04) * mm, v(-6.86, -36.04) * mm, v(-7.6, -35.55) * mm, v(-8.54, -34.56) * mm]});
            skFitSpline(sketch, "E607", {"points": [v(-9.2, -33.84) * mm, v(-9.4, -33.63) * mm, v(-9.57, -33.42) * mm, v(-9.7, -33.2) * mm]});
            skFitSpline(sketch, "E608", {"points": [v(-9.7, -33.2) * mm, v(-9.83, -32.97) * mm, v(-9.9, -32.75) * mm, v(-9.9, -32.53) * mm]});
            skFitSpline(sketch, "E609", {"points": [v(-9.9, -32.53) * mm, v(-9.9, -32.47) * mm, v(-9.87, -32.39) * mm, v(-9.82, -32.3) * mm]});
            skFitSpline(sketch, "E610", {"points": [v(-9.37, -32.84) * mm, v(-9.1, -33.22) * mm, v(-8.78, -33.61) * mm, v(-8.4, -34) * mm]});
            skFitSpline(sketch, "E611", {"points": [v(-8.4, -34) * mm, v(-8.03, -34.4) * mm, v(-7.7, -34.6) * mm, v(-7.43, -34.6) * mm]});
            skFitSpline(sketch, "E612", {"points": [v(-7.43, -34.6) * mm, v(-7.11, -34.6) * mm, v(-6.95, -34.26) * mm, v(-6.95, -33.58) * mm]});
            skFitSpline(sketch, "E613", {"points": [v(-6.95, -33.58) * mm, v(-6.95, -33.1) * mm, v(-7.02, -32.5) * mm, v(-7.15, -31.8) * mm]});
            skFitSpline(sketch, "E614", {"points": [v(-7.15, -31.8) * mm, v(-7.29, -31.1) * mm, v(-7.44, -30.58) * mm, v(-7.62, -30.24) * mm]});
            skFitSpline(sketch, "E615", {"points": [v(-7.62, -30.24) * mm, v(-7.8, -29.9) * mm, v(-7.98, -29.68) * mm, v(-8.18, -29.57) * mm]});
            skFitSpline(sketch, "E616", {"points": [v(-8.18, -29.57) * mm, v(-8.38, -29.46) * mm, v(-8.61, -29.4) * mm, v(-8.87, -29.4) * mm]});
            skFitSpline(sketch, "E617", {"points": [v(-11.29, -29.14) * mm, v(-11.29, -28.69) * mm, v(-11.15, -28.46) * mm, v(-10.86, -28.46) * mm]});
            skFitSpline(sketch, "E618", {"points": [v(-10.86, -28.46) * mm, v(-10.7, -28.46) * mm, v(-10.52, -28.55) * mm, v(-10.3, -28.73) * mm]});
            skFitSpline(sketch, "E619", {"points": [v(-10.3, -28.73) * mm, v(-10.11, -28.93) * mm, v(-9.95, -29.18) * mm, v(-9.83, -29.48) * mm]});
            skFitSpline(sketch, "E620", {"points": [v(-9.83, -29.48) * mm, v(-9.7, -29.78) * mm, v(-9.62, -30.05) * mm, v(-9.57, -30.28) * mm]});
            skFitSpline(sketch, "E621", {"points": [v(-9.57, -30.28) * mm, v(-9.52, -30.5) * mm, v(-9.48, -30.78) * mm, v(-9.46, -31.1) * mm]});
            skFitSpline(sketch, "E622", {"points": [v(-8.99, -35.3) * mm, v(-8.99, -35.79) * mm, v(-9.1, -36.03) * mm, v(-9.32, -36.03) * mm]});
            skFitSpline(sketch, "E623", {"points": [v(-9.32, -36.03) * mm, v(-9.52, -36.03) * mm, v(-9.8, -35.88) * mm, v(-10.17, -35.6) * mm]});
            skFitSpline(sketch, "E624", {"points": [v(-10.17, -35.6) * mm, v(-10.53, -35.35) * mm, v(-11.12, -34.87) * mm, v(-11.93, -34.14) * mm]});
            skFitSpline(sketch, "E625", {"points": [v(-11.93, -34.14) * mm, v(-11.99, -34.08) * mm, v(-12.02, -34.03) * mm, v(-12.05, -33.99) * mm]});
            skFitSpline(sketch, "E626", {"points": [v(-12.05, -33.99) * mm, v(-12.08, -33.95) * mm, v(-12.1, -33.91) * mm, v(-12.1, -33.87) * mm]});
            skFitSpline(sketch, "E627", {"points": [v(-12.1, -33.87) * mm, v(-12.1, -33.85) * mm, v(-12.08, -33.81) * mm, v(-12.01, -33.78) * mm]});
            skFitSpline(sketch, "E628", {"points": [v(-12.01, -33.78) * mm, v(-11.92, -33.78) * mm, v(-11.8, -33.82) * mm, v(-11.67, -33.91) * mm]});
            skFitSpline(sketch, "E629", {"points": [v(-11.67, -33.91) * mm, v(-11.54, -34) * mm, v(-11.41, -34.1) * mm, v(-11.3, -34.18) * mm]});
            skFitSpline(sketch, "E630", {"points": [v(-11.3, -34.18) * mm, v(-11.18, -34.27) * mm, v(-11.07, -34.36) * mm, v(-10.98, -34.45) * mm]});
            skFitSpline(sketch, "E631", {"points": [v(-10.58, -34.75) * mm, v(-10.56, -34.73) * mm, v(-10.55, -34.71) * mm, v(-10.53, -34.68) * mm]});
            skFitSpline(sketch, "E632", {"points": [v(-10.53, -34.68) * mm, v(-10.5, -34.65) * mm, v(-10.5, -34.6) * mm, v(-10.5, -34.51) * mm]});
            skFitSpline(sketch, "E633", {"points": [v(-15.04, -33.96) * mm, v(-14.75, -34.25) * mm, v(-14.54, -34.4) * mm, v(-14.4, -34.4) * mm]});
            skFitSpline(sketch, "E634", {"points": [v(-14.4, -34.4) * mm, v(-14.24, -34.4) * mm, v(-14.16, -34.18) * mm, v(-14.16, -33.74) * mm]});
            skFitSpline(sketch, "E635", {"points": [v(-15.08, -27.43) * mm, v(-15.46, -25.24) * mm, v(-15.66, -23.89) * mm, v(-15.66, -23.38) * mm]});
            skFitSpline(sketch, "E636", {"points": [v(-15.66, -23.38) * mm, v(-15.66, -22.98) * mm, v(-15.57, -22.78) * mm, v(-15.39, -22.78) * mm]});
            skFitSpline(sketch, "E637", {"points": [v(-15.39, -22.78) * mm, v(-15.26, -22.78) * mm, v(-15.13, -22.83) * mm, v(-15, -22.92) * mm]});
            skFitSpline(sketch, "E638", {"points": [v(-14.03, -23.56) * mm, v(-13.56, -23.88) * mm, v(-13.19, -24.12) * mm, v(-12.9, -24.28) * mm]});
            skFitSpline(sketch, "E639", {"points": [v(-12.9, -24.28) * mm, v(-12.62, -24.44) * mm, v(-12.48, -24.6) * mm, v(-12.48, -24.72) * mm]});
            skFitSpline(sketch, "E640", {"points": [v(-12.48, -24.72) * mm, v(-12.5, -24.82) * mm, v(-12.55, -24.87) * mm, v(-12.63, -24.87) * mm]});
            skFitSpline(sketch, "E641", {"points": [v(-12.86, -24.8) * mm, v(-13.36, -24.5) * mm, v(-13.64, -24.35) * mm, v(-13.72, -24.35) * mm]});
            skFitSpline(sketch, "E642", {"points": [v(-13.72, -24.35) * mm, v(-13.85, -24.35) * mm, v(-13.91, -24.49) * mm, v(-13.91, -24.76) * mm]});
            skFitSpline(sketch, "E643", {"points": [v(-12.55, -35.39) * mm, v(-12.55, -35.9) * mm, v(-12.67, -36.16) * mm, v(-12.9, -36.16) * mm]});
            skFitSpline(sketch, "E644", {"points": [v(-12.9, -36.16) * mm, v(-13.25, -36.16) * mm, v(-13.82, -35.77) * mm, v(-14.6, -35) * mm]});
            skFitSpline(sketch, "E645", {"points": [v(-14.6, -35) * mm, v(-15.37, -34.22) * mm, v(-15.75, -33.78) * mm, v(-15.75, -33.66) * mm]});
            skFitSpline(sketch, "E646", {"points": [v(-15.75, -33.66) * mm, v(-15.75, -33.57) * mm, v(-15.7, -33.52) * mm, v(-15.6, -33.52) * mm]});
            skFitSpline(sketch, "E647", {"points": [v(-15.6, -33.52) * mm, v(-15.5, -33.52) * mm, v(-15.32, -33.67) * mm, v(-15.04, -33.96) * mm]});
            skFitSpline(sketch, "E648", {"points": [v(-18.37, -28.75) * mm, v(-17.76, -28.96) * mm, v(-17.33, -29.2) * mm, v(-17.05, -29.48) * mm]});
            skFitSpline(sketch, "E649", {"points": [v(-17.05, -29.48) * mm, v(-16.78, -29.75) * mm, v(-16.52, -30.34) * mm, v(-16.26, -31.23) * mm]});
            skFitSpline(sketch, "E650", {"points": [v(-16.26, -31.23) * mm, v(-16, -32.12) * mm, v(-15.87, -32.85) * mm, v(-15.87, -33.43) * mm]});
            skFitSpline(sketch, "E651", {"points": [v(-15.87, -33.43) * mm, v(-15.87, -34.16) * mm, v(-16.02, -34.78) * mm, v(-16.32, -35.3) * mm]});
            skFitSpline(sketch, "E652", {"points": [v(-16.32, -35.3) * mm, v(-16.61, -35.8) * mm, v(-17.03, -36.06) * mm, v(-17.56, -36.06) * mm]});
            skFitSpline(sketch, "E653", {"points": [v(-17.56, -36.06) * mm, v(-18.1, -36.06) * mm, v(-18.62, -35.9) * mm, v(-19.13, -35.54) * mm]});
            skFitSpline(sketch, "E654", {"points": [v(-20.12, -34.9) * mm, v(-20.3, -34.79) * mm, v(-20.45, -34.68) * mm, v(-20.58, -34.57) * mm]});
            skFitSpline(sketch, "E655", {"points": [v(-20.58, -34.57) * mm, v(-20.71, -34.46) * mm, v(-20.84, -34.34) * mm, v(-20.97, -34.2) * mm]});
            skFitSpline(sketch, "E656", {"points": [v(-20.97, -34.2) * mm, v(-21.1, -34.08) * mm, v(-21.2, -33.86) * mm, v(-21.26, -33.55) * mm]});
            skFitSpline(sketch, "E657", {"points": [v(-21.79, -30.84) * mm, v(-21.79, -30.26) * mm, v(-21.54, -29.7) * mm, v(-21.06, -29.17) * mm]});
            skFitSpline(sketch, "E658", {"points": [v(-21.06, -29.17) * mm, v(-20.57, -28.63) * mm, v(-20.16, -28.37) * mm, v(-19.8, -28.37) * mm]});
            skFitSpline(sketch, "E659", {"points": [v(-18, -30.05) * mm, v(-18.1, -29.8) * mm, v(-18.2, -29.6) * mm, v(-18.3, -29.45) * mm]});
            skFitSpline(sketch, "E660", {"points": [v(-18.3, -29.45) * mm, v(-18.42, -29.32) * mm, v(-18.52, -29.24) * mm, v(-18.58, -29.2) * mm]});
            skFitSpline(sketch, "E661", {"points": [v(-18.58, -29.2) * mm, v(-18.63, -29.16) * mm, v(-18.7, -29.11) * mm, v(-18.79, -29.05) * mm]});
            skFitSpline(sketch, "E662", {"points": [v(-18.79, -29.05) * mm, v(-18.87, -29) * mm, v(-18.97, -28.97) * mm, v(-19.1, -28.97) * mm]});
            skFitSpline(sketch, "E663", {"points": [v(-19.1, -28.97) * mm, v(-19.3, -28.97) * mm, v(-19.5, -29.07) * mm, v(-19.68, -29.29) * mm]});
            skFitSpline(sketch, "E664", {"points": [v(-19.68, -29.29) * mm, v(-19.86, -29.5) * mm, v(-19.96, -29.73) * mm, v(-20, -29.97) * mm]});
            skFitSpline(sketch, "E665", {"points": [v(-20, -29.97) * mm, v(-20.1, -30.43) * mm, v(-20.16, -30.87) * mm, v(-20.16, -31.31) * mm]});
            skFitSpline(sketch, "E666", {"points": [v(-20.16, -31.31) * mm, v(-20.16, -32.05) * mm, v(-20.07, -32.74) * mm, v(-19.9, -33.39) * mm]});
            skFitSpline(sketch, "E667", {"points": [v(-19.9, -33.39) * mm, v(-19.74, -34.03) * mm, v(-19.53, -34.46) * mm, v(-19.3, -34.68) * mm]});
            skFitSpline(sketch, "E668", {"points": [v(-19.3, -34.68) * mm, v(-19.05, -34.9) * mm, v(-18.89, -35) * mm, v(-18.8, -35) * mm]});
            skFitSpline(sketch, "E669", {"points": [v(-18.8, -35) * mm, v(-18.64, -35) * mm, v(-18.45, -34.92) * mm, v(-18.2, -34.77) * mm]});
            skFitSpline(sketch, "E670", {"points": [v(-18.2, -34.77) * mm, v(-17.97, -34.61) * mm, v(-17.78, -34.33) * mm, v(-17.65, -33.91) * mm]});
            skFitSpline(sketch, "E671", {"points": [v(-17.65, -33.91) * mm, v(-17.5, -33.5) * mm, v(-17.44, -33.04) * mm, v(-17.44, -32.53) * mm]});
            skFitSpline(sketch, "E672", {"points": [v(-17.44, -32.53) * mm, v(-17.44, -32.15) * mm, v(-17.47, -31.86) * mm, v(-17.54, -31.66) * mm]});
            skFitSpline(sketch, "E673", {"points": [v(-24.75, -28.75) * mm, v(-24.15, -28.96) * mm, v(-23.7, -29.2) * mm, v(-23.43, -29.48) * mm]});
            skFitSpline(sketch, "E674", {"points": [v(-23.43, -29.48) * mm, v(-23.16, -29.75) * mm, v(-22.9, -30.34) * mm, v(-22.64, -31.23) * mm]});
            skFitSpline(sketch, "E675", {"points": [v(-22.64, -31.23) * mm, v(-22.38, -32.12) * mm, v(-22.25, -32.85) * mm, v(-22.25, -33.43) * mm]});
            skFitSpline(sketch, "E676", {"points": [v(-22.25, -33.43) * mm, v(-22.25, -34.16) * mm, v(-22.4, -34.78) * mm, v(-22.7, -35.3) * mm]});
            skFitSpline(sketch, "E677", {"points": [v(-22.7, -35.3) * mm, v(-23, -35.8) * mm, v(-23.4, -36.06) * mm, v(-23.94, -36.06) * mm]});
            skFitSpline(sketch, "E678", {"points": [v(-23.94, -36.06) * mm, v(-24.48, -36.06) * mm, v(-25, -35.9) * mm, v(-25.5, -35.54) * mm]});
            skFitSpline(sketch, "E679", {"points": [v(-26.5, -34.9) * mm, v(-26.68, -34.79) * mm, v(-26.83, -34.68) * mm, v(-26.96, -34.57) * mm]});
            skFitSpline(sketch, "E680", {"points": [v(-26.96, -34.57) * mm, v(-27.1, -34.46) * mm, v(-27.22, -34.34) * mm, v(-27.35, -34.2) * mm]});
            skFitSpline(sketch, "E681", {"points": [v(-27.35, -34.2) * mm, v(-27.48, -34.08) * mm, v(-27.58, -33.86) * mm, v(-27.64, -33.55) * mm]});
            skFitSpline(sketch, "E682", {"points": [v(-28.17, -30.84) * mm, v(-28.17, -30.26) * mm, v(-27.92, -29.7) * mm, v(-27.44, -29.17) * mm]});
            skFitSpline(sketch, "E683", {"points": [v(-27.44, -29.17) * mm, v(-26.95, -28.63) * mm, v(-26.54, -28.37) * mm, v(-26.19, -28.37) * mm]});
            skFitSpline(sketch, "E684", {"points": [v(-24.38, -30.05) * mm, v(-24.48, -29.8) * mm, v(-24.57, -29.6) * mm, v(-24.68, -29.45) * mm]});
            skFitSpline(sketch, "E685", {"points": [v(-24.68, -29.45) * mm, v(-24.8, -29.32) * mm, v(-24.9, -29.24) * mm, v(-24.96, -29.2) * mm]});
            skFitSpline(sketch, "E686", {"points": [v(-24.96, -29.2) * mm, v(-25.02, -29.16) * mm, v(-25.09, -29.11) * mm, v(-25.17, -29.05) * mm]});
            skFitSpline(sketch, "E687", {"points": [v(-25.17, -29.05) * mm, v(-25.25, -29) * mm, v(-25.35, -28.97) * mm, v(-25.47, -28.97) * mm]});
            skFitSpline(sketch, "E688", {"points": [v(-25.47, -28.97) * mm, v(-25.7, -28.97) * mm, v(-25.89, -29.07) * mm, v(-26.06, -29.29) * mm]});
            skFitSpline(sketch, "E689", {"points": [v(-26.06, -29.29) * mm, v(-26.24, -29.5) * mm, v(-26.34, -29.73) * mm, v(-26.38, -29.97) * mm]});
            skFitSpline(sketch, "E690", {"points": [v(-26.38, -29.97) * mm, v(-26.49, -30.43) * mm, v(-26.54, -30.87) * mm, v(-26.54, -31.31) * mm]});
            skFitSpline(sketch, "E691", {"points": [v(-26.54, -31.31) * mm, v(-26.54, -32.05) * mm, v(-26.45, -32.74) * mm, v(-26.29, -33.39) * mm]});
            skFitSpline(sketch, "E692", {"points": [v(-26.29, -33.39) * mm, v(-26.12, -34.03) * mm, v(-25.91, -34.46) * mm, v(-25.67, -34.68) * mm]});
            skFitSpline(sketch, "E693", {"points": [v(-25.67, -34.68) * mm, v(-25.43, -34.9) * mm, v(-25.27, -35) * mm, v(-25.18, -35) * mm]});
            skFitSpline(sketch, "E694", {"points": [v(-25.18, -35) * mm, v(-25.02, -35) * mm, v(-24.83, -34.92) * mm, v(-24.59, -34.77) * mm]});
            skFitSpline(sketch, "E695", {"points": [v(-24.59, -34.77) * mm, v(-24.35, -34.61) * mm, v(-24.16, -34.33) * mm, v(-24.03, -33.91) * mm]});
            skFitSpline(sketch, "E696", {"points": [v(-24.03, -33.91) * mm, v(-23.9, -33.5) * mm, v(-23.82, -33.04) * mm, v(-23.82, -32.53) * mm]});
            skFitSpline(sketch, "E697", {"points": [v(-23.82, -32.53) * mm, v(-23.82, -32.15) * mm, v(-23.85, -31.86) * mm, v(-23.92, -31.66) * mm]});
            skFitSpline(sketch, "E698", {"points": [v(-29.49, -30.2) * mm, v(-29.52, -29.94) * mm, v(-29.64, -29.77) * mm, v(-29.82, -29.71) * mm]});
            skFitSpline(sketch, "E699", {"points": [v(-29.82, -29.71) * mm, v(-30.01, -29.65) * mm, v(-30.34, -29.63) * mm, v(-30.82, -29.63) * mm]});
            skFitSpline(sketch, "E700", {"points": [v(-32.6, -29.59) * mm, v(-32.3, -30.26) * mm, v(-31.89, -31) * mm, v(-31.38, -31.82) * mm]});
            skFitSpline(sketch, "E701", {"points": [v(-31.38, -31.82) * mm, v(-30.87, -32.63) * mm, v(-30.37, -33.32) * mm, v(-29.9, -33.87) * mm]});
            skFitSpline(sketch, "E702", {"points": [v(-29.9, -33.87) * mm, v(-29.43, -34.43) * mm, v(-28.81, -35.04) * mm, v(-28.05, -35.7) * mm]});
            skFitSpline(sketch, "E703", {"points": [v(-28.34, -36) * mm, v(-28.77, -35.68) * mm, v(-29.35, -35.2) * mm, v(-30.1, -34.53) * mm]});
            skFitSpline(sketch, "E704", {"points": [v(-30.1, -34.53) * mm, v(-30.84, -33.87) * mm, v(-31.53, -33.1) * mm, v(-32.16, -32.19) * mm]});
            skFitSpline(sketch, "E705", {"points": [v(-34.28, -28.64) * mm, v(-34.3, -28.6) * mm, v(-34.31, -28.54) * mm, v(-34.31, -28.46) * mm]});
            skFitSpline(sketch, "E706", {"points": [v(-34.31, -28.46) * mm, v(-34.31, -28.37) * mm, v(-34.27, -28.33) * mm, v(-34.18, -28.33) * mm]});
            skFitSpline(sketch, "E707", {"points": [v(-34.02, -28.38) * mm, v(-33.87, -28.5) * mm, v(-33.58, -28.56) * mm, v(-33.17, -28.56) * mm]});
            skFitSpline(sketch, "E708", {"points": [v(-30.4, -28.23) * mm, v(-30.06, -28.23) * mm, v(-29.8, -28.29) * mm, v(-29.6, -28.4) * mm]});
            skFitSpline(sketch, "E709", {"points": [v(-29.6, -28.4) * mm, v(-29.4, -28.52) * mm, v(-29.28, -28.65) * mm, v(-29.22, -28.8) * mm]});
            skFitSpline(sketch, "E710", {"points": [v(-29.22, -28.8) * mm, v(-29.17, -28.93) * mm, v(-29.12, -29.12) * mm, v(-29.1, -29.33) * mm]});
            skFitSpline(sketch, "E711", {"points": [v(-29.02, -30) * mm, v(-29.02, -30.4) * mm, v(-29.1, -30.61) * mm, v(-29.23, -30.61) * mm]});
            skFitSpline(sketch, "E712", {"points": [v(-29.23, -30.61) * mm, v(-29.36, -30.61) * mm, v(-29.45, -30.48) * mm, v(-29.49, -30.2) * mm]});
            skFitSpline(sketch, "E713", {"points": [v(-28.22, -35.85) * mm, v(-28.25, -35.88) * mm, v(-28.3, -35.9) * mm, v(-28.4, -35.95) * mm]});
            skFitSpline(sketch, "E714", {"points": [v(-29.27, -35.27) * mm, v(-29.45, -35.15) * mm, v(-29.62, -35.1) * mm, v(-29.78, -35.1) * mm]});
            skFitSpline(sketch, "E715", {"points": [v(-29.78, -35.1) * mm, v(-30.02, -35.1) * mm, v(-30.42, -35.3) * mm, v(-30.96, -35.68) * mm]});
            skFitSpline(sketch, "E716", {"points": [v(-30.96, -35.68) * mm, v(-31.27, -35.94) * mm, v(-31.63, -36.06) * mm, v(-32.03, -36.06) * mm]});
            skFitSpline(sketch, "E717", {"points": [v(-32.03, -36.06) * mm, v(-32.43, -36.06) * mm, v(-32.81, -35.93) * mm, v(-33.19, -35.66) * mm]});
            skFitSpline(sketch, "E718", {"points": [v(-33.19, -35.66) * mm, v(-33.56, -35.4) * mm, v(-33.83, -35.1) * mm, v(-33.98, -34.79) * mm]});
            skFitSpline(sketch, "E719", {"points": [v(-33.98, -34.79) * mm, v(-34.14, -34.47) * mm, v(-34.22, -34.25) * mm, v(-34.22, -34.12) * mm]});
            skFitSpline(sketch, "E720", {"points": [v(-34.22, -34.12) * mm, v(-34.22, -34.07) * mm, v(-34.19, -34.02) * mm, v(-34.12, -33.97) * mm]});
            skFitSpline(sketch, "E721", {"points": [v(-34.12, -33.97) * mm, v(-34, -33.97) * mm, v(-33.9, -34.05) * mm, v(-33.83, -34.22) * mm]});
            skFitSpline(sketch, "E722", {"points": [v(-33.83, -34.22) * mm, v(-33.56, -34.62) * mm, v(-33.23, -34.82) * mm, v(-32.84, -34.82) * mm]});
            skFitSpline(sketch, "E723", {"points": [v(-32.84, -34.82) * mm, v(-32.71, -34.82) * mm, v(-32.6, -34.81) * mm, v(-32.48, -34.78) * mm]});
            skFitSpline(sketch, "E724", {"points": [v(-32.48, -34.78) * mm, v(-32.37, -34.76) * mm, v(-32.25, -34.72) * mm, v(-32.12, -34.67) * mm]});
            skFitSpline(sketch, "E725", {"points": [v(-30.22, -33.8) * mm, v(-30.1, -33.74) * mm, v(-29.98, -33.72) * mm, v(-29.83, -33.72) * mm]});
            skFitSpline(sketch, "E726", {"points": [v(-29.83, -33.72) * mm, v(-29.5, -33.72) * mm, v(-29.2, -33.86) * mm, v(-28.91, -34.13) * mm]});
            skFitSpline(sketch, "E727", {"points": [v(-28.91, -34.13) * mm, v(-28.64, -34.41) * mm, v(-28.45, -34.73) * mm, v(-28.36, -35.08) * mm]});
            skFitSpline(sketch, "E728", {"points": [v(-39.76, -29.33) * mm, v(-39.87, -29.28) * mm, v(-39.95, -29.19) * mm, v(-40.03, -29.06) * mm]});
            skFitSpline(sketch, "E729", {"points": [v(-40.03, -29.06) * mm, v(-40.1, -28.94) * mm, v(-40.13, -28.82) * mm, v(-40.13, -28.72) * mm]});
            skFitSpline(sketch, "E730", {"points": [v(-40.13, -28.72) * mm, v(-40.13, -28.52) * mm, v(-39.94, -28.42) * mm, v(-39.55, -28.42) * mm]});
            skFitSpline(sketch, "E731", {"points": [v(-38.08, -28.55) * mm, v(-37.73, -28.55) * mm, v(-37.4, -28.64) * mm, v(-37.09, -28.8) * mm]});
            skFitSpline(sketch, "E732", {"points": [v(-37.09, -28.8) * mm, v(-36.78, -28.96) * mm, v(-36.43, -29.24) * mm, v(-36.06, -29.65) * mm]});
            skFitSpline(sketch, "E733", {"points": [v(-36.06, -29.65) * mm, v(-35.68, -30.06) * mm, v(-35.4, -30.54) * mm, v(-35.19, -31.09) * mm]});
            skFitSpline(sketch, "E734", {"points": [v(-35.19, -31.09) * mm, v(-34.98, -31.63) * mm, v(-34.83, -32.08) * mm, v(-34.74, -32.43) * mm]});
            skFitSpline(sketch, "E735", {"points": [v(-34.74, -32.43) * mm, v(-34.65, -32.78) * mm, v(-34.58, -33.1) * mm, v(-34.54, -33.38) * mm]});
            skFitSpline(sketch, "E736", {"points": [v(-34.54, -33.38) * mm, v(-34.5, -33.67) * mm, v(-34.46, -33.9) * mm, v(-34.45, -34.1) * mm]});
            skFitSpline(sketch, "E737", {"points": [v(-34.45, -34.1) * mm, v(-34.44, -34.28) * mm, v(-34.43, -34.42) * mm, v(-34.43, -34.5) * mm]});
            skFitSpline(sketch, "E738", {"points": [v(-34.43, -34.5) * mm, v(-34.43, -35.53) * mm, v(-34.71, -36.04) * mm, v(-35.28, -36.04) * mm]});
            skFitSpline(sketch, "E739", {"points": [v(-35.28, -36.04) * mm, v(-35.81, -36.04) * mm, v(-36.55, -35.55) * mm, v(-37.5, -34.56) * mm]});
            skFitSpline(sketch, "E740", {"points": [v(-38.15, -33.84) * mm, v(-38.36, -33.63) * mm, v(-38.53, -33.42) * mm, v(-38.66, -33.2) * mm]});
            skFitSpline(sketch, "E741", {"points": [v(-38.66, -33.2) * mm, v(-38.79, -32.97) * mm, v(-38.85, -32.75) * mm, v(-38.85, -32.53) * mm]});
            skFitSpline(sketch, "E742", {"points": [v(-38.85, -32.53) * mm, v(-38.85, -32.47) * mm, v(-38.83, -32.39) * mm, v(-38.77, -32.3) * mm]});
            skFitSpline(sketch, "E743", {"points": [v(-38.33, -32.84) * mm, v(-38.06, -33.22) * mm, v(-37.73, -33.61) * mm, v(-37.36, -34) * mm]});
            skFitSpline(sketch, "E744", {"points": [v(-37.36, -34) * mm, v(-36.98, -34.4) * mm, v(-36.66, -34.6) * mm, v(-36.39, -34.6) * mm]});
            skFitSpline(sketch, "E745", {"points": [v(-36.39, -34.6) * mm, v(-36.07, -34.6) * mm, v(-35.9, -34.26) * mm, v(-35.9, -33.58) * mm]});
            skFitSpline(sketch, "E746", {"points": [v(-35.9, -33.58) * mm, v(-35.9, -33.1) * mm, v(-35.97, -32.5) * mm, v(-36.1, -31.8) * mm]});
            skFitSpline(sketch, "E747", {"points": [v(-36.1, -31.8) * mm, v(-36.24, -31.1) * mm, v(-36.4, -30.58) * mm, v(-36.57, -30.24) * mm]});
            skFitSpline(sketch, "E748", {"points": [v(-36.57, -30.24) * mm, v(-36.75, -29.9) * mm, v(-36.94, -29.68) * mm, v(-37.14, -29.57) * mm]});
            skFitSpline(sketch, "E749", {"points": [v(-37.14, -29.57) * mm, v(-37.34, -29.46) * mm, v(-37.57, -29.4) * mm, v(-37.82, -29.4) * mm]});
            skFitSpline(sketch, "E750", {"points": [v(-40.24, -29.14) * mm, v(-40.24, -28.69) * mm, v(-40.1, -28.46) * mm, v(-39.82, -28.46) * mm]});
            skFitSpline(sketch, "E751", {"points": [v(-39.82, -28.46) * mm, v(-39.66, -28.46) * mm, v(-39.48, -28.55) * mm, v(-39.26, -28.73) * mm]});
            skFitSpline(sketch, "E752", {"points": [v(-39.26, -28.73) * mm, v(-39.07, -28.93) * mm, v(-38.9, -29.18) * mm, v(-38.79, -29.48) * mm]});
            skFitSpline(sketch, "E753", {"points": [v(-38.79, -29.48) * mm, v(-38.66, -29.78) * mm, v(-38.58, -30.05) * mm, v(-38.53, -30.28) * mm]});
            skFitSpline(sketch, "E754", {"points": [v(-38.53, -30.28) * mm, v(-38.47, -30.5) * mm, v(-38.44, -30.78) * mm, v(-38.41, -31.1) * mm]});
            skFitSpline(sketch, "E755", {"points": [v(-37.94, -35.3) * mm, v(-37.94, -35.79) * mm, v(-38.05, -36.03) * mm, v(-38.27, -36.03) * mm]});
            skFitSpline(sketch, "E756", {"points": [v(-38.27, -36.03) * mm, v(-38.48, -36.03) * mm, v(-38.76, -35.88) * mm, v(-39.12, -35.6) * mm]});
            skFitSpline(sketch, "E757", {"points": [v(-39.12, -35.6) * mm, v(-39.49, -35.35) * mm, v(-40.07, -34.87) * mm, v(-40.89, -34.14) * mm]});
            skFitSpline(sketch, "E758", {"points": [v(-40.89, -34.14) * mm, v(-40.94, -34.08) * mm, v(-40.98, -34.03) * mm, v(-41, -33.99) * mm]});
            skFitSpline(sketch, "E759", {"points": [v(-41, -33.99) * mm, v(-41.03, -33.95) * mm, v(-41.05, -33.91) * mm, v(-41.06, -33.87) * mm]});
            skFitSpline(sketch, "E760", {"points": [v(-41.06, -33.87) * mm, v(-41.06, -33.85) * mm, v(-41.03, -33.81) * mm, v(-40.97, -33.78) * mm]});
            skFitSpline(sketch, "E761", {"points": [v(-40.97, -33.78) * mm, v(-40.88, -33.78) * mm, v(-40.76, -33.82) * mm, v(-40.63, -33.91) * mm]});
            skFitSpline(sketch, "E762", {"points": [v(-40.63, -33.91) * mm, v(-40.5, -34) * mm, v(-40.37, -34.1) * mm, v(-40.25, -34.18) * mm]});
            skFitSpline(sketch, "E763", {"points": [v(-40.25, -34.18) * mm, v(-40.13, -34.27) * mm, v(-40.03, -34.36) * mm, v(-39.94, -34.45) * mm]});
            skFitSpline(sketch, "E764", {"points": [v(-39.53, -34.75) * mm, v(-39.52, -34.73) * mm, v(-39.5, -34.71) * mm, v(-39.48, -34.68) * mm]});
            skFitSpline(sketch, "E765", {"points": [v(-39.48, -34.68) * mm, v(-39.46, -34.65) * mm, v(-39.45, -34.6) * mm, v(-39.45, -34.51) * mm]});
            skFitSpline(sketch, "E766", {"points": [v(22.3, -54) * mm, v(22.86, -53.32) * mm, v(23.74, -52.78) * mm, v(24.93, -52.38) * mm]});
            skFitSpline(sketch, "E767", {"points": [v(24.93, -52.38) * mm, v(25.54, -52.18) * mm, v(26.1, -52.02) * mm, v(26.63, -51.9) * mm]});
            skFitSpline(sketch, "E768", {"points": [v(26.63, -51.9) * mm, v(27.16, -51.8) * mm, v(27.71, -51.68) * mm, v(28.28, -51.56) * mm]});
            skFitSpline(sketch, "E769", {"points": [v(28.28, -51.56) * mm, v(29.15, -51.37) * mm, v(29.75, -51.17) * mm, v(30.06, -50.94) * mm]});
            skFitSpline(sketch, "E770", {"points": [v(30.06, -50.94) * mm, v(30.37, -50.72) * mm, v(30.53, -50.4) * mm, v(30.53, -49.98) * mm]});
            skFitSpline(sketch, "E771", {"points": [v(30.53, -49.98) * mm, v(30.53, -49.7) * mm, v(30.43, -49.45) * mm, v(30.24, -49.23) * mm]});
            skFitSpline(sketch, "E772", {"points": [v(30.24, -49.23) * mm, v(30.04, -49.02) * mm, v(29.8, -48.86) * mm, v(29.54, -48.75) * mm]});
            skFitSpline(sketch, "E773", {"points": [v(29.54, -48.75) * mm, v(29.23, -48.62) * mm, v(28.91, -48.53) * mm, v(28.58, -48.49) * mm]});
            skFitSpline(sketch, "E774", {"points": [v(28.58, -48.49) * mm, v(28.25, -48.44) * mm, v(27.92, -48.42) * mm, v(27.58, -48.42) * mm]});
            skFitSpline(sketch, "E775", {"points": [v(27.58, -48.42) * mm, v(26.63, -48.42) * mm, v(25.7, -48.6) * mm, v(24.8, -48.94) * mm]});
            skFitSpline(sketch, "E776", {"points": [v(24.8, -48.94) * mm, v(23.88, -49.28) * mm, v(23.11, -49.7) * mm, v(22.49, -50.22) * mm]});
            skFitSpline(sketch, "E777", {"points": [v(22.06, -46.56) * mm, v(22.8, -46.25) * mm, v(23.66, -46) * mm, v(24.66, -45.8) * mm]});
            skFitSpline(sketch, "E778", {"points": [v(24.66, -45.8) * mm, v(25.66, -45.6) * mm, v(26.67, -45.5) * mm, v(27.7, -45.5) * mm]});
            skFitSpline(sketch, "E779", {"points": [v(27.7, -45.5) * mm, v(29.74, -45.5) * mm, v(31.41, -45.96) * mm, v(32.71, -46.9) * mm]});
            skFitSpline(sketch, "E780", {"points": [v(32.71, -46.9) * mm, v(34.01, -47.83) * mm, v(34.66, -49.04) * mm, v(34.66, -50.52) * mm]});
            skFitSpline(sketch, "E781", {"points": [v(34.66, -50.52) * mm, v(34.66, -51.62) * mm, v(34.38, -52.55) * mm, v(33.8, -53.29) * mm]});
            skFitSpline(sketch, "E782", {"points": [v(33.8, -53.29) * mm, v(33.23, -54.03) * mm, v(32.28, -54.62) * mm, v(30.97, -55.06) * mm]});
            skFitSpline(sketch, "E783", {"points": [v(30.97, -55.06) * mm, v(30.4, -55.25) * mm, v(29.79, -55.4) * mm, v(29.13, -55.53) * mm]});
            skFitSpline(sketch, "E784", {"points": [v(29.13, -55.53) * mm, v(28.48, -55.66) * mm, v(27.86, -55.79) * mm, v(27.28, -55.93) * mm]});
            skFitSpline(sketch, "E785", {"points": [v(27.28, -55.93) * mm, v(26.72, -56.07) * mm, v(26.3, -56.26) * mm, v(26, -56.51) * mm]});
            skFitSpline(sketch, "E786", {"points": [v(26, -56.51) * mm, v(25.72, -56.77) * mm, v(25.57, -57.07) * mm, v(25.57, -57.42) * mm]});
            skFitSpline(sketch, "E787", {"points": [v(25.57, -57.42) * mm, v(25.57, -57.8) * mm, v(25.67, -58.08) * mm, v(25.87, -58.27) * mm]});
            skFitSpline(sketch, "E788", {"points": [v(25.87, -58.27) * mm, v(26.07, -58.46) * mm, v(26.32, -58.62) * mm, v(26.63, -58.75) * mm]});
            skFitSpline(sketch, "E789", {"points": [v(26.63, -58.75) * mm, v(26.88, -58.85) * mm, v(27.2, -58.92) * mm, v(27.6, -58.96) * mm]});
            skFitSpline(sketch, "E790", {"points": [v(27.6, -58.96) * mm, v(28, -59) * mm, v(28.32, -59.03) * mm, v(28.56, -59.03) * mm]});
            skFitSpline(sketch, "E791", {"points": [v(28.56, -59.03) * mm, v(29.51, -59.03) * mm, v(30.5, -58.85) * mm, v(31.53, -58.48) * mm]});
            skFitSpline(sketch, "E792", {"points": [v(31.53, -58.48) * mm, v(32.56, -58.12) * mm, v(33.49, -57.6) * mm, v(34.32, -56.92) * mm]});
            skFitSpline(sketch, "E793", {"points": [v(34.76, -60.73) * mm, v(33.92, -61.1) * mm, v(33.02, -61.38) * mm, v(32.06, -61.62) * mm]});
            skFitSpline(sketch, "E794", {"points": [v(32.06, -61.62) * mm, v(31.1, -61.85) * mm, v(29.98, -61.96) * mm, v(28.7, -61.96) * mm]});
            skFitSpline(sketch, "E795", {"points": [v(28.7, -61.96) * mm, v(26.46, -61.96) * mm, v(24.7, -61.47) * mm, v(23.4, -60.5) * mm]});
            skFitSpline(sketch, "E796", {"points": [v(23.4, -60.5) * mm, v(22.1, -59.52) * mm, v(21.44, -58.24) * mm, v(21.44, -56.68) * mm]});
            skFitSpline(sketch, "E797", {"points": [v(21.44, -56.68) * mm, v(21.44, -55.58) * mm, v(21.72, -54.7) * mm, v(22.3, -54) * mm]});
            skSolve(sketch);
        }
        {
            var Q0;
            Q0=qSketchRegion(id+"F0",true);
            extrude(context, id + "F2", {"entities" : qUnion([Q0]), "depth" : 0.8 * mm, "offsetDistance" : 25 * mm, "symmetric" : true});
        }
        {
            var Q0;
            Q0=qSketchRegion(id+"F1",true);
            var Q1;
            Q1=makeQuery(id+"F2.opExtrude","CAP_FACE",FACE,{"disambiguationData":[OSD([sQuery(id+"F0.wireOp",EDGE,"E0.bottom"),sQuery(id+"F0.wireOp",EDGE,"E0.top"),sQuery(id+"F0.wireOp",EDGE,"E0.left"),sQuery(id+"F0.wireOp",EDGE,"E0.right"),sQuery(id+"F0.wireOp",EDGE,"E1"),sQuery(id+"F0.wireOp",EDGE,"E2.filletArc"),sQuery(id+"F0.wireOp",EDGE,"E3.filletArc"),sQuery(id+"F0.wireOp",EDGE,"E4.filletArc"),sQuery(id+"F0.wireOp",EDGE,"E5.filletArc")])],"isStart":true});
            extrude(context, id + "F3", {"entities" : qUnion([Q0]), "operationType" : NewBodyOperationType.REMOVE, "endBound" : BoundingType.UP_TO_SURFACE, "oppositeDirection" : true, "depth" : 25 * mm, "endBoundEntityFace" : qUnion([Q1]), "offsetDistance" : 25 * mm});
        }
        {
            var Q0;
            Q0=qSketchRegion(id+"F1",true);
            var Q1;
            {var subQ27=sQuery(id+"F0.wireOp",EDGE,"E4.filletArc");var subQ29=sQuery(id+"F0.wireOp",EDGE,"E0.left");var subQ31=sQuery(id+"F0.wireOp",EDGE,"E0.top");var subQ32=sQuery(id+"F0.wireOp",EDGE,"E0.right");var subQ33=sQuery(id+"F0.wireOp",EDGE,"E1");var subQ34=sQuery(id+"F0.wireOp",EDGE,"E0.bottom");var subQ37=sQuery(id+"F0.wireOp",EDGE,"E2.filletArc");var subQ39=sQuery(id+"F0.wireOp",EDGE,"E5.filletArc");var subQ40=sQuery(id+"F0.wireOp",EDGE,"E3.filletArc");Q1=makeQuery(id+"F3.boolean.opBoolean","SPLIT",FACE,{"disambiguationData":[TD([makeQuery(id+"F2.opExtrude","SWEPT_FACE",FACE,{"disambiguationData":[OSD([subQ34])]})])],"derivedFrom":makeQuery(id+"F2.opExtrude","CAP_FACE",FACE,{"disambiguationData":[OSD([subQ34,subQ31,subQ29,subQ32,subQ33,subQ37,subQ40,subQ27,subQ39])],"isStart":true})});}
            extrude(context, id + "F4", {"entities" : qUnion([Q0]), "endBound" : BoundingType.UP_TO_SURFACE, "oppositeDirection" : true, "depth" : 25 * mm, "endBoundEntityFace" : qUnion([Q1]), "offsetDistance" : 25 * mm});
        }
        {
            var Q0;
            Q0=makeQuery(id+"F2.opExtrude","CAP_FACE",FACE,{"disambiguationData":[OSD([sQuery(id+"F0.wireOp",EDGE,"E0.bottom"),sQuery(id+"F0.wireOp",EDGE,"E0.top"),sQuery(id+"F0.wireOp",EDGE,"E0.left"),sQuery(id+"F0.wireOp",EDGE,"E0.right"),sQuery(id+"F0.wireOp",EDGE,"E1"),sQuery(id+"F0.wireOp",EDGE,"E2.filletArc"),sQuery(id+"F0.wireOp",EDGE,"E3.filletArc"),sQuery(id+"F0.wireOp",EDGE,"E4.filletArc"),sQuery(id+"F0.wireOp",EDGE,"E5.filletArc"),sQuery(id+"F0.wireOp",EDGE,"E6"),sQuery(id+"F0.wireOp",EDGE,"E7.filletArc"),sQuery(id+"F0.wireOp",EDGE,"E8"),sQuery(id+"F0.wireOp",EDGE,"E9.filletArc")])],"isStart":false});
            var sketch = newSketch(context, id + "F5", { "sketchPlane" : qUnion([Q0])});
            skText(sketch, "E798", { "text": "Grapeman", "fontName": "RobotoSlab-Bold.ttf"});
            const initialGuessF5  = {"E798": [-0.042, -0.062, 1, 0, 0.01227]};
            skSetInitialGuess(sketch, initialGuessF5);
            skSolve(sketch);
        }
        {
            var Q0;
            Q0=qSketchRegion(id+"F5",true);
            extrude(context, id + "F6", {"entities" : qUnion([Q0]), "operationType" : NewBodyOperationType.ADD, "depth" : 1 * mm, "offsetDistance" : 25 * mm});
        }
    });
